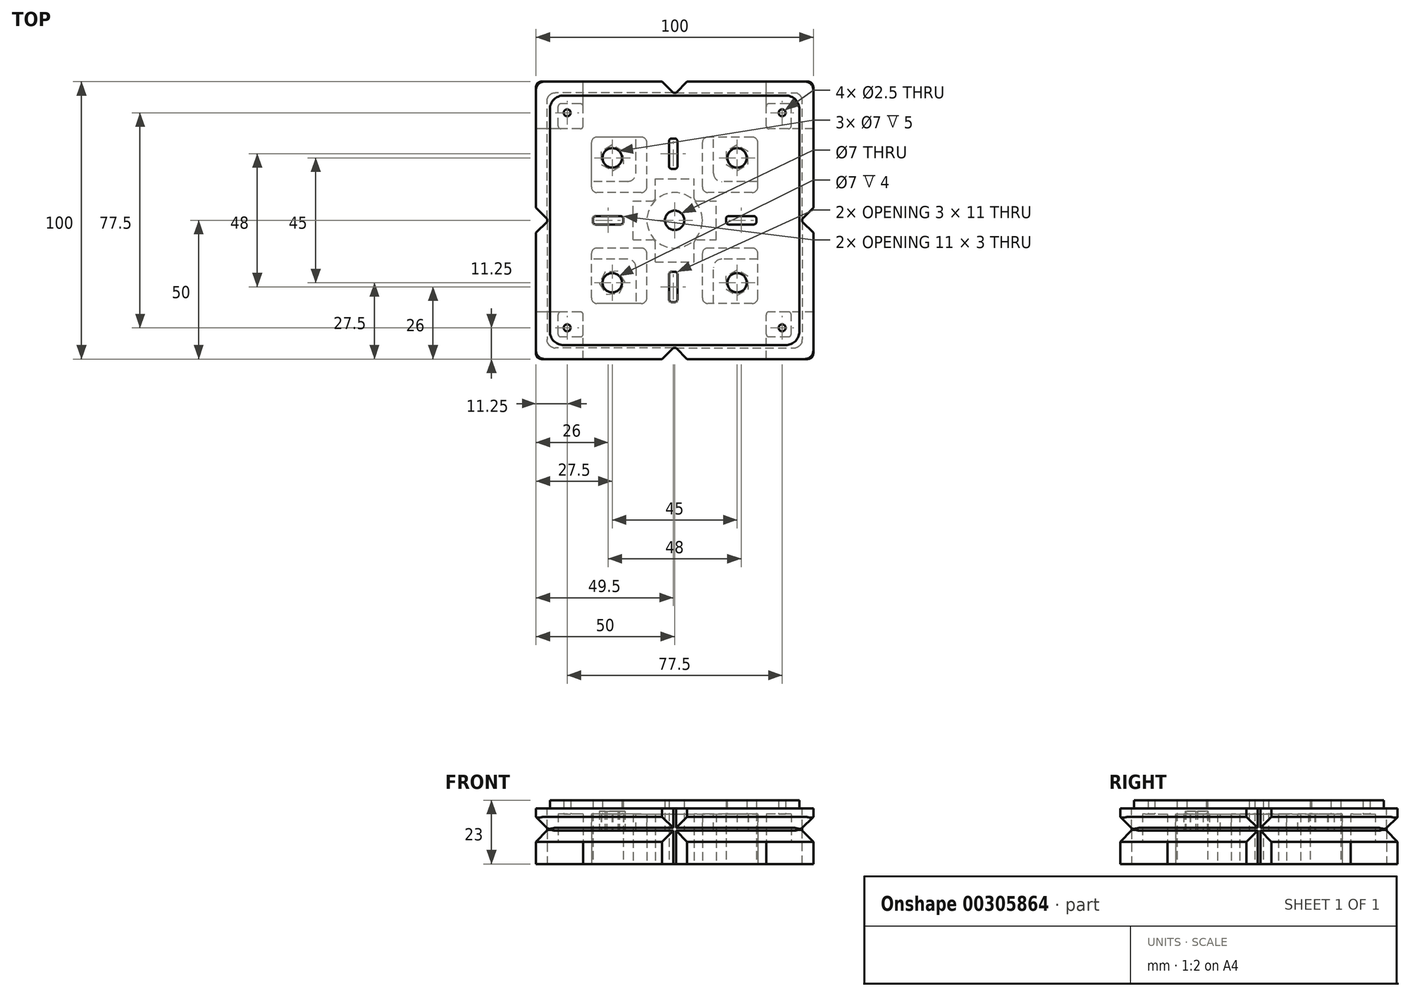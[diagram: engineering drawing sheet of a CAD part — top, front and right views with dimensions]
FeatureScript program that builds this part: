
annotation { "Feature Type Name" : "Feature", "Feature Type Description" : "" }
export const myFeature = defineFeature(function(context is Context, id is Id, definition is map)
    precondition{}
    {
        {
            var Q0;
            Q0=qCreatedBy(makeId("Top.planeOp"),FACE);
            var sketch = newSketch(context, id + "F0", { "sketchPlane" : qUnion([Q0])});
            skLineSegment(sketch, "E0.bottom", {"start": v(50, 50) * mm, "end": v(-50, 50) * mm});
            skLineSegment(sketch, "E0.top", {"start": v(50, -50) * mm, "end": v(-50, -50) * mm});
            skLineSegment(sketch, "E0.left", {"start": v(50, 50) * mm, "end": v(50, -50) * mm});
            skLineSegment(sketch, "E0.right", {"start": v(-50, 50) * mm, "end": v(-50, -50) * mm});
            skPoint(sketch, "E0.middle", {"position": v(0, 0) * mm});
            skCircle(sketch, "E1", {"center": v(0, 0) * mm, "radius": 3.5 * mm});
            skLineSegment(sketch, "E2.bottom", {"start": v(-4.5, -50) * mm, "end": v(4.5, -50) * mm});
            skLineSegment(sketch, "E2.top", {"start": v(-4.5, -46) * mm, "end": v(4.5, -46) * mm});
            skLineSegment(sketch, "E2.left", {"start": v(-4.5, -50) * mm, "end": v(-4.5, -46) * mm});
            skLineSegment(sketch, "E2.right", {"start": v(4.5, -50) * mm, "end": v(4.5, -46) * mm});
            skSolve(sketch);
        }
        {
            var Q0;
            Q0=qSketchRegion(id+"F0",true);
            extrude(context, id + "F1", {"entities" : qUnion([Q0]), "depth" : 20 * mm});
        }
        {
            var Q0;
            Q0=makeQuery(id+"F1.opExtrude","CAP_FACE",FACE,{"disambiguationData":[OSD([sQuery(id+"F0.wireOp",EDGE,"E0.bottom"),sQuery(id+"F0.wireOp",EDGE,"E0.top"),sQuery(id+"F0.wireOp",EDGE,"E0.left"),sQuery(id+"F0.wireOp",EDGE,"E0.right")])],"isStart":false});
            var sketch = newSketch(context, id + "F2", { "sketchPlane" : qUnion([Q0])});
            skLineSegment(sketch, "E3.bottom", {"start": v(45, 45) * mm, "end": v(-45, 45) * mm});
            skLineSegment(sketch, "E3.top", {"start": v(45, -45) * mm, "end": v(-45, -45) * mm});
            skLineSegment(sketch, "E3.left", {"start": v(45, 45) * mm, "end": v(45, -45) * mm});
            skLineSegment(sketch, "E3.right", {"start": v(-45, 45) * mm, "end": v(-45, -45) * mm});
            skPoint(sketch, "E3.middle", {"position": v(0, 0) * mm});
            skCircle(sketch, "E4", {"center": v(0, 0) * mm, "radius": 3.5 * mm});
            skLineSegment(sketch, "E5.bottom", {"start": v(-2, 29.5) * mm, "end": v(1, 29.5) * mm});
            skLineSegment(sketch, "E5.top", {"start": v(-2, 18.5) * mm, "end": v(1, 18.5) * mm});
            skLineSegment(sketch, "E5.left", {"start": v(-2, 29.5) * mm, "end": v(-2, 18.5) * mm});
            skLineSegment(sketch, "E5.right", {"start": v(1, 29.5) * mm, "end": v(1, 18.5) * mm});
            skLineSegment(sketch, "E6.bottom", {"start": v(-2, -18.5) * mm, "end": v(1, -18.5) * mm});
            skLineSegment(sketch, "E6.top", {"start": v(-2, -29.5) * mm, "end": v(1, -29.5) * mm});
            skLineSegment(sketch, "E6.left", {"start": v(-2, -18.5) * mm, "end": v(-2, -29.5) * mm});
            skLineSegment(sketch, "E6.right", {"start": v(1, -18.5) * mm, "end": v(1, -29.5) * mm});
            skLineSegment(sketch, "E7.bottom", {"start": v(-29.5, -1.5) * mm, "end": v(-29.5, 1.5) * mm});
            skLineSegment(sketch, "E7.top", {"start": v(-18.5, -1.5) * mm, "end": v(-18.5, 1.5) * mm});
            skLineSegment(sketch, "E7.left", {"start": v(-29.5, -1.5) * mm, "end": v(-18.5, -1.5) * mm});
            skLineSegment(sketch, "E7.right", {"start": v(-29.5, 1.5) * mm, "end": v(-18.5, 1.5) * mm});
            skLineSegment(sketch, "E8.bottom", {"start": v(18.5, -1.5) * mm, "end": v(18.5, 1.5) * mm});
            skLineSegment(sketch, "E8.top", {"start": v(29.5, -1.5) * mm, "end": v(29.5, 1.5) * mm});
            skLineSegment(sketch, "E8.left", {"start": v(18.5, -1.5) * mm, "end": v(29.5, -1.5) * mm});
            skLineSegment(sketch, "E8.right", {"start": v(18.5, 1.5) * mm, "end": v(29.5, 1.5) * mm});
            skCircle(sketch, "E9", {"center": v(22.5, -22.5) * mm, "radius": 3.5 * mm});
            skCircle(sketch, "E10", {"center": v(-22.5, -22.5) * mm, "radius": 3.5 * mm});
            skCircle(sketch, "E11", {"center": v(-22.5, 22.5) * mm, "radius": 3.5 * mm});
            skCircle(sketch, "E12", {"center": v(22.5, 22.5) * mm, "radius": 3.5 * mm});
            skCircle(sketch, "E13", {"center": v(-38.75, 38.75) * mm, "radius": 1.25 * mm});
            skCircle(sketch, "E14", {"center": v(38.75, 38.75) * mm, "radius": 1.25 * mm});
            skCircle(sketch, "E15", {"center": v(38.75, -38.75) * mm, "radius": 1.25 * mm});
            skCircle(sketch, "E16", {"center": v(-38.75, -38.75) * mm, "radius": 1.25 * mm});
            skSolve(sketch);
        }
        {
            var Q0;
            Q0=qSketchRegion(id+"F2",true);
            extrude(context, id + "F3", {"entities" : qUnion([Q0]), "operationType" : NewBodyOperationType.ADD, "depth" : 3 * mm});
        }
        {
            var Q0;
            Q0=makeQuery(id+"F3.boolean.opBoolean","SPLIT",FACE,{"disambiguationData":[TD([makeQuery(id+"F3.opExtrude","SWEPT_FACE",FACE,{"disambiguationData":[OSD([sQuery(id+"F2.wireOp",EDGE,"E5.bottom")])]})])],"derivedFrom":makeQuery(id+"F1.opExtrude","CAP_FACE",FACE,{"disambiguationData":[OSD([sQuery(id+"F0.wireOp",EDGE,"E0.bottom"),sQuery(id+"F0.wireOp",EDGE,"E0.top"),sQuery(id+"F0.wireOp",EDGE,"E0.left"),sQuery(id+"F0.wireOp",EDGE,"E0.right"),sQuery(id+"F0.wireOp",EDGE,"E1")])],"isStart":false})});
            extrude(context, id + "F4", {"entities" : qUnion([Q0]), "operationType" : NewBodyOperationType.REMOVE, "oppositeDirection" : true, "depth" : 25 * mm});
        }
        {
            var Q0;
            Q0=makeQuery(id+"F3.boolean.opBoolean","SPLIT",FACE,{"disambiguationData":[TD([makeQuery(id+"F3.opExtrude","SWEPT_FACE",FACE,{"disambiguationData":[OSD([sQuery(id+"F2.wireOp",EDGE,"E7.bottom")])]})])],"derivedFrom":makeQuery(id+"F1.opExtrude","CAP_FACE",FACE,{"disambiguationData":[OSD([sQuery(id+"F0.wireOp",EDGE,"E0.bottom"),sQuery(id+"F0.wireOp",EDGE,"E0.top"),sQuery(id+"F0.wireOp",EDGE,"E0.left"),sQuery(id+"F0.wireOp",EDGE,"E0.right"),sQuery(id+"F0.wireOp",EDGE,"E1")])],"isStart":false})});
            extrude(context, id + "F5", {"entities" : qUnion([Q0]), "operationType" : NewBodyOperationType.REMOVE, "oppositeDirection" : true, "depth" : 25 * mm});
        }
        {
            var Q0;
            Q0=makeQuery(id+"F3.boolean.opBoolean","SPLIT",FACE,{"disambiguationData":[TD([makeQuery(id+"F3.opExtrude","SWEPT_FACE",FACE,{"disambiguationData":[OSD([sQuery(id+"F2.wireOp",EDGE,"E6.bottom")])]})])],"derivedFrom":makeQuery(id+"F1.opExtrude","CAP_FACE",FACE,{"disambiguationData":[OSD([sQuery(id+"F0.wireOp",EDGE,"E0.bottom"),sQuery(id+"F0.wireOp",EDGE,"E0.top"),sQuery(id+"F0.wireOp",EDGE,"E0.left"),sQuery(id+"F0.wireOp",EDGE,"E0.right"),sQuery(id+"F0.wireOp",EDGE,"E1")])],"isStart":false})});
            extrude(context, id + "F6", {"entities" : qUnion([Q0]), "operationType" : NewBodyOperationType.REMOVE, "oppositeDirection" : true, "depth" : 25 * mm});
        }
        {
            var Q0;
            Q0=makeQuery(id+"F3.boolean.opBoolean","SPLIT",FACE,{"disambiguationData":[TD([makeQuery(id+"F3.opExtrude","SWEPT_FACE",FACE,{"disambiguationData":[OSD([sQuery(id+"F2.wireOp",EDGE,"E8.bottom")])]})])],"derivedFrom":makeQuery(id+"F1.opExtrude","CAP_FACE",FACE,{"disambiguationData":[OSD([sQuery(id+"F0.wireOp",EDGE,"E0.bottom"),sQuery(id+"F0.wireOp",EDGE,"E0.top"),sQuery(id+"F0.wireOp",EDGE,"E0.left"),sQuery(id+"F0.wireOp",EDGE,"E0.right"),sQuery(id+"F0.wireOp",EDGE,"E1")])],"isStart":false})});
            extrude(context, id + "F7", {"entities" : qUnion([Q0]), "operationType" : NewBodyOperationType.REMOVE, "oppositeDirection" : true, "depth" : 25 * mm});
        }
        {
            var Q0;
            {var subQ0=sQuery(id+"F2.wireOp",EDGE,"E5.left");var subQ1=sQuery(id+"F2.wireOp",EDGE,"E5.bottom");Q0=makeQuery(id+"F4.boolean.opBoolean","MERGE",EDGE,{"derivedFrom":[makeQuery(id+"F3.opExtrude","SWEPT_EDGE",EDGE,{"disambiguationData":[OSD([subQ1,subQ0])]}),makeQuery(id+"F4.opExtrude","SWEPT_EDGE",EDGE,{"disambiguationData":[OSD([subQ1,subQ0])]})]});}
            var Q1;
            {var subQ0=sQuery(id+"F2.wireOp",EDGE,"E5.right");var subQ1=sQuery(id+"F2.wireOp",EDGE,"E5.bottom");Q1=makeQuery(id+"F4.boolean.opBoolean","MERGE",EDGE,{"derivedFrom":[makeQuery(id+"F3.opExtrude","SWEPT_EDGE",EDGE,{"disambiguationData":[OSD([subQ1,subQ0])]}),makeQuery(id+"F4.opExtrude","SWEPT_EDGE",EDGE,{"disambiguationData":[OSD([subQ1,subQ0])]})]});}
            var Q2;
            {var subQ0=sQuery(id+"F2.wireOp",EDGE,"E5.right");var subQ1=sQuery(id+"F2.wireOp",EDGE,"E5.top");Q2=makeQuery(id+"F4.boolean.opBoolean","MERGE",EDGE,{"derivedFrom":[makeQuery(id+"F3.opExtrude","SWEPT_EDGE",EDGE,{"disambiguationData":[OSD([subQ1,subQ0])]}),makeQuery(id+"F4.opExtrude","SWEPT_EDGE",EDGE,{"disambiguationData":[OSD([subQ1,subQ0])]})]});}
            var Q3;
            {var subQ0=sQuery(id+"F2.wireOp",EDGE,"E5.left");var subQ1=sQuery(id+"F2.wireOp",EDGE,"E5.top");Q3=makeQuery(id+"F4.boolean.opBoolean","MERGE",EDGE,{"derivedFrom":[makeQuery(id+"F3.opExtrude","SWEPT_EDGE",EDGE,{"disambiguationData":[OSD([subQ1,subQ0])]}),makeQuery(id+"F4.opExtrude","SWEPT_EDGE",EDGE,{"disambiguationData":[OSD([subQ1,subQ0])]})]});}
            var Q4;
            {var subQ0=sQuery(id+"F2.wireOp",EDGE,"E8.right");var subQ1=sQuery(id+"F2.wireOp",EDGE,"E8.bottom");Q4=makeQuery(id+"F7.boolean.opBoolean","MERGE",EDGE,{"derivedFrom":[makeQuery(id+"F3.opExtrude","SWEPT_EDGE",EDGE,{"disambiguationData":[OSD([subQ1,subQ0])]}),makeQuery(id+"F7.opExtrude","SWEPT_EDGE",EDGE,{"disambiguationData":[OSD([subQ1,subQ0])]})]});}
            var Q5;
            {var subQ0=sQuery(id+"F2.wireOp",EDGE,"E8.left");var subQ1=sQuery(id+"F2.wireOp",EDGE,"E8.bottom");Q5=makeQuery(id+"F7.boolean.opBoolean","MERGE",EDGE,{"derivedFrom":[makeQuery(id+"F3.opExtrude","SWEPT_EDGE",EDGE,{"disambiguationData":[OSD([subQ1,subQ0])]}),makeQuery(id+"F7.opExtrude","SWEPT_EDGE",EDGE,{"disambiguationData":[OSD([subQ1,subQ0])]})]});}
            var Q6;
            {var subQ0=sQuery(id+"F2.wireOp",EDGE,"E8.left");var subQ1=sQuery(id+"F2.wireOp",EDGE,"E8.top");Q6=makeQuery(id+"F7.boolean.opBoolean","MERGE",EDGE,{"derivedFrom":[makeQuery(id+"F3.opExtrude","SWEPT_EDGE",EDGE,{"disambiguationData":[OSD([subQ1,subQ0])]}),makeQuery(id+"F7.opExtrude","SWEPT_EDGE",EDGE,{"disambiguationData":[OSD([subQ1,subQ0])]})]});}
            var Q7;
            {var subQ0=sQuery(id+"F2.wireOp",EDGE,"E8.right");var subQ1=sQuery(id+"F2.wireOp",EDGE,"E8.top");Q7=makeQuery(id+"F7.boolean.opBoolean","MERGE",EDGE,{"derivedFrom":[makeQuery(id+"F3.opExtrude","SWEPT_EDGE",EDGE,{"disambiguationData":[OSD([subQ1,subQ0])]}),makeQuery(id+"F7.opExtrude","SWEPT_EDGE",EDGE,{"disambiguationData":[OSD([subQ1,subQ0])]})]});}
            var Q8;
            {var subQ0=sQuery(id+"F2.wireOp",EDGE,"E6.right");var subQ1=sQuery(id+"F2.wireOp",EDGE,"E6.bottom");Q8=makeQuery(id+"F6.boolean.opBoolean","MERGE",EDGE,{"derivedFrom":[makeQuery(id+"F3.opExtrude","SWEPT_EDGE",EDGE,{"disambiguationData":[OSD([subQ1,subQ0])]}),makeQuery(id+"F6.opExtrude","SWEPT_EDGE",EDGE,{"disambiguationData":[OSD([subQ1,subQ0])]})]});}
            var Q9;
            {var subQ0=sQuery(id+"F2.wireOp",EDGE,"E6.left");var subQ1=sQuery(id+"F2.wireOp",EDGE,"E6.bottom");Q9=makeQuery(id+"F6.boolean.opBoolean","MERGE",EDGE,{"derivedFrom":[makeQuery(id+"F3.opExtrude","SWEPT_EDGE",EDGE,{"disambiguationData":[OSD([subQ1,subQ0])]}),makeQuery(id+"F6.opExtrude","SWEPT_EDGE",EDGE,{"disambiguationData":[OSD([subQ1,subQ0])]})]});}
            var Q10;
            {var subQ0=sQuery(id+"F2.wireOp",EDGE,"E6.left");var subQ1=sQuery(id+"F2.wireOp",EDGE,"E6.top");Q10=makeQuery(id+"F6.boolean.opBoolean","MERGE",EDGE,{"derivedFrom":[makeQuery(id+"F3.opExtrude","SWEPT_EDGE",EDGE,{"disambiguationData":[OSD([subQ1,subQ0])]}),makeQuery(id+"F6.opExtrude","SWEPT_EDGE",EDGE,{"disambiguationData":[OSD([subQ1,subQ0])]})]});}
            var Q11;
            {var subQ0=sQuery(id+"F2.wireOp",EDGE,"E6.right");var subQ1=sQuery(id+"F2.wireOp",EDGE,"E6.top");Q11=makeQuery(id+"F6.boolean.opBoolean","MERGE",EDGE,{"derivedFrom":[makeQuery(id+"F3.opExtrude","SWEPT_EDGE",EDGE,{"disambiguationData":[OSD([subQ1,subQ0])]}),makeQuery(id+"F6.opExtrude","SWEPT_EDGE",EDGE,{"disambiguationData":[OSD([subQ1,subQ0])]})]});}
            var Q12;
            {var subQ0=sQuery(id+"F2.wireOp",EDGE,"E7.left");var subQ1=sQuery(id+"F2.wireOp",EDGE,"E7.bottom");Q12=makeQuery(id+"F5.boolean.opBoolean","MERGE",EDGE,{"derivedFrom":[makeQuery(id+"F3.opExtrude","SWEPT_EDGE",EDGE,{"disambiguationData":[OSD([subQ1,subQ0])]}),makeQuery(id+"F5.opExtrude","SWEPT_EDGE",EDGE,{"disambiguationData":[OSD([subQ1,subQ0])]})]});}
            var Q13;
            {var subQ0=sQuery(id+"F2.wireOp",EDGE,"E7.right");var subQ1=sQuery(id+"F2.wireOp",EDGE,"E7.top");Q13=makeQuery(id+"F5.boolean.opBoolean","MERGE",EDGE,{"derivedFrom":[makeQuery(id+"F3.opExtrude","SWEPT_EDGE",EDGE,{"disambiguationData":[OSD([subQ1,subQ0])]}),makeQuery(id+"F5.opExtrude","SWEPT_EDGE",EDGE,{"disambiguationData":[OSD([subQ1,subQ0])]})]});}
            var Q14;
            {var subQ0=sQuery(id+"F2.wireOp",EDGE,"E7.left");var subQ1=sQuery(id+"F2.wireOp",EDGE,"E7.top");Q14=makeQuery(id+"F5.boolean.opBoolean","MERGE",EDGE,{"derivedFrom":[makeQuery(id+"F3.opExtrude","SWEPT_EDGE",EDGE,{"disambiguationData":[OSD([subQ1,subQ0])]}),makeQuery(id+"F5.opExtrude","SWEPT_EDGE",EDGE,{"disambiguationData":[OSD([subQ1,subQ0])]})]});}
            var Q15;
            {var subQ0=sQuery(id+"F2.wireOp",EDGE,"E7.right");var subQ1=sQuery(id+"F2.wireOp",EDGE,"E7.bottom");Q15=makeQuery(id+"F5.boolean.opBoolean","MERGE",EDGE,{"derivedFrom":[makeQuery(id+"F3.opExtrude","SWEPT_EDGE",EDGE,{"disambiguationData":[OSD([subQ1,subQ0])]}),makeQuery(id+"F5.opExtrude","SWEPT_EDGE",EDGE,{"disambiguationData":[OSD([subQ1,subQ0])]})]});}
            fillet(context, id + "F8", {"entities" : qUnion([Q0, Q1, Q2, Q3, Q4, Q5, Q6, Q7, Q8, Q9, Q10, Q11, Q12, Q13, Q14, Q15]), "radius" : 1 * mm, "tangentPropagation" : true, "allowEdgeOverflow" : false});
        }
        {
            var Q0;
            Q0=makeQuery(id+"F3.boolean.opBoolean","SPLIT",FACE,{"disambiguationData":[TD([makeQuery(id+"F3.opExtrude","SWEPT_FACE",FACE,{"disambiguationData":[OSD([sQuery(id+"F2.wireOp",EDGE,"E11")])]})])],"derivedFrom":makeQuery(id+"F1.opExtrude","CAP_FACE",FACE,{"disambiguationData":[OSD([sQuery(id+"F0.wireOp",EDGE,"E0.bottom"),sQuery(id+"F0.wireOp",EDGE,"E0.top"),sQuery(id+"F0.wireOp",EDGE,"E0.left"),sQuery(id+"F0.wireOp",EDGE,"E0.right"),sQuery(id+"F0.wireOp",EDGE,"E1")])],"isStart":false})});
            var Q1;
            Q1=makeQuery(id+"F3.boolean.opBoolean","SPLIT",FACE,{"disambiguationData":[TD([makeQuery(id+"F3.opExtrude","SWEPT_FACE",FACE,{"disambiguationData":[OSD([sQuery(id+"F2.wireOp",EDGE,"E12")])]})])],"derivedFrom":makeQuery(id+"F1.opExtrude","CAP_FACE",FACE,{"disambiguationData":[OSD([sQuery(id+"F0.wireOp",EDGE,"E0.bottom"),sQuery(id+"F0.wireOp",EDGE,"E0.top"),sQuery(id+"F0.wireOp",EDGE,"E0.left"),sQuery(id+"F0.wireOp",EDGE,"E0.right"),sQuery(id+"F0.wireOp",EDGE,"E1")])],"isStart":false})});
            var Q2;
            Q2=makeQuery(id+"F3.boolean.opBoolean","SPLIT",FACE,{"disambiguationData":[TD([makeQuery(id+"F3.opExtrude","SWEPT_FACE",FACE,{"disambiguationData":[OSD([sQuery(id+"F2.wireOp",EDGE,"E9")])]})])],"derivedFrom":makeQuery(id+"F1.opExtrude","CAP_FACE",FACE,{"disambiguationData":[OSD([sQuery(id+"F0.wireOp",EDGE,"E0.bottom"),sQuery(id+"F0.wireOp",EDGE,"E0.top"),sQuery(id+"F0.wireOp",EDGE,"E0.left"),sQuery(id+"F0.wireOp",EDGE,"E0.right"),sQuery(id+"F0.wireOp",EDGE,"E1")])],"isStart":false})});
            var Q3;
            Q3=makeQuery(id+"F3.boolean.opBoolean","SPLIT",FACE,{"disambiguationData":[TD([makeQuery(id+"F3.opExtrude","SWEPT_FACE",FACE,{"disambiguationData":[OSD([sQuery(id+"F2.wireOp",EDGE,"E10")])]})])],"derivedFrom":makeQuery(id+"F1.opExtrude","CAP_FACE",FACE,{"disambiguationData":[OSD([sQuery(id+"F0.wireOp",EDGE,"E0.bottom"),sQuery(id+"F0.wireOp",EDGE,"E0.top"),sQuery(id+"F0.wireOp",EDGE,"E0.left"),sQuery(id+"F0.wireOp",EDGE,"E0.right"),sQuery(id+"F0.wireOp",EDGE,"E1")])],"isStart":false})});
            extrude(context, id + "F9", {"entities" : qUnion([Q0, Q1, Q2, Q3]), "operationType" : NewBodyOperationType.REMOVE, "oppositeDirection" : true, "depth" : 25 * mm});
        }
        {
            var Q0;
            Q0=makeQuery(id+"F3.boolean.opBoolean","SPLIT",FACE,{"disambiguationData":[TD([makeQuery(id+"F3.opExtrude","SWEPT_FACE",FACE,{"disambiguationData":[OSD([sQuery(id+"F2.wireOp",EDGE,"E15")])]})])],"derivedFrom":makeQuery(id+"F1.opExtrude","CAP_FACE",FACE,{"disambiguationData":[OSD([sQuery(id+"F0.wireOp",EDGE,"E0.bottom"),sQuery(id+"F0.wireOp",EDGE,"E0.top"),sQuery(id+"F0.wireOp",EDGE,"E0.left"),sQuery(id+"F0.wireOp",EDGE,"E0.right"),sQuery(id+"F0.wireOp",EDGE,"E1")])],"isStart":false})});
            var Q1;
            Q1=makeQuery(id+"F3.boolean.opBoolean","SPLIT",FACE,{"disambiguationData":[TD([makeQuery(id+"F3.opExtrude","SWEPT_FACE",FACE,{"disambiguationData":[OSD([sQuery(id+"F2.wireOp",EDGE,"E16")])]})])],"derivedFrom":makeQuery(id+"F1.opExtrude","CAP_FACE",FACE,{"disambiguationData":[OSD([sQuery(id+"F0.wireOp",EDGE,"E0.bottom"),sQuery(id+"F0.wireOp",EDGE,"E0.top"),sQuery(id+"F0.wireOp",EDGE,"E0.left"),sQuery(id+"F0.wireOp",EDGE,"E0.right"),sQuery(id+"F0.wireOp",EDGE,"E1")])],"isStart":false})});
            var Q2;
            Q2=makeQuery(id+"F3.boolean.opBoolean","SPLIT",FACE,{"disambiguationData":[TD([makeQuery(id+"F3.opExtrude","SWEPT_FACE",FACE,{"disambiguationData":[OSD([sQuery(id+"F2.wireOp",EDGE,"E13")])]})])],"derivedFrom":makeQuery(id+"F1.opExtrude","CAP_FACE",FACE,{"disambiguationData":[OSD([sQuery(id+"F0.wireOp",EDGE,"E0.bottom"),sQuery(id+"F0.wireOp",EDGE,"E0.top"),sQuery(id+"F0.wireOp",EDGE,"E0.left"),sQuery(id+"F0.wireOp",EDGE,"E0.right"),sQuery(id+"F0.wireOp",EDGE,"E1")])],"isStart":false})});
            var Q3;
            Q3=makeQuery(id+"F3.boolean.opBoolean","SPLIT",FACE,{"disambiguationData":[TD([makeQuery(id+"F3.opExtrude","SWEPT_FACE",FACE,{"disambiguationData":[OSD([sQuery(id+"F2.wireOp",EDGE,"E14")])]})])],"derivedFrom":makeQuery(id+"F1.opExtrude","CAP_FACE",FACE,{"disambiguationData":[OSD([sQuery(id+"F0.wireOp",EDGE,"E0.bottom"),sQuery(id+"F0.wireOp",EDGE,"E0.top"),sQuery(id+"F0.wireOp",EDGE,"E0.left"),sQuery(id+"F0.wireOp",EDGE,"E0.right"),sQuery(id+"F0.wireOp",EDGE,"E1")])],"isStart":false})});
            extrude(context, id + "F10", {"entities" : qUnion([Q0, Q1, Q2, Q3]), "operationType" : NewBodyOperationType.REMOVE, "oppositeDirection" : true, "depth" : 25 * mm});
        }
        {
            var Q0;
            Q0=makeQuery(id+"F3.opExtrude","SWEPT_EDGE",EDGE,{"disambiguationData":[OSD([sQuery(id+"F2.wireOp",EDGE,"E3.top"),sQuery(id+"F2.wireOp",EDGE,"E3.right")])]});
            var Q1;
            Q1=makeQuery(id+"F3.opExtrude","SWEPT_EDGE",EDGE,{"disambiguationData":[OSD([sQuery(id+"F2.wireOp",EDGE,"E3.top"),sQuery(id+"F2.wireOp",EDGE,"E3.left")])]});
            var Q2;
            Q2=makeQuery(id+"F3.opExtrude","SWEPT_EDGE",EDGE,{"disambiguationData":[OSD([sQuery(id+"F2.wireOp",EDGE,"E3.bottom"),sQuery(id+"F2.wireOp",EDGE,"E3.right")])]});
            var Q3;
            Q3=makeQuery(id+"F3.opExtrude","SWEPT_EDGE",EDGE,{"disambiguationData":[OSD([sQuery(id+"F2.wireOp",EDGE,"E3.bottom"),sQuery(id+"F2.wireOp",EDGE,"E3.left")])]});
            fillet(context, id + "F11", {"entities" : qUnion([Q0, Q1, Q2, Q3]), "radius" : 5 * mm, "tangentPropagation" : true, "allowEdgeOverflow" : false});
        }
        {
            var Q0;
            Q0=makeQuery(id+"F1.opExtrude","CAP_FACE",FACE,{"disambiguationData":[OSD([sQuery(id+"F0.wireOp",EDGE,"E0.bottom"),sQuery(id+"F0.wireOp",EDGE,"E0.top"),sQuery(id+"F0.wireOp",EDGE,"E0.left"),sQuery(id+"F0.wireOp",EDGE,"E0.right"),sQuery(id+"F0.wireOp",EDGE,"E1"),sQuery(id+"F0.wireOp",EDGE,"E2.bottom")])],"isStart":true});
            var sketch = newSketch(context, id + "F12", { "sketchPlane" : qUnion([Q0])});
            skLineSegment(sketch, "E17.bottom", {"start": v(-4.5, 50) * mm, "end": v(4.5, 50) * mm});
            skLineSegment(sketch, "E17.top", {"start": v(-4.5, 46) * mm, "end": v(4.5, 46) * mm});
            skLineSegment(sketch, "E17.left", {"start": v(-4.5, 50) * mm, "end": v(-4.5, 46) * mm});
            skLineSegment(sketch, "E17.right", {"start": v(4.5, 50) * mm, "end": v(4.5, 46) * mm});
            skLineSegment(sketch, "E18.bottom", {"start": v(-46, 4.5) * mm, "end": v(-50, 4.5) * mm});
            skLineSegment(sketch, "E18.top", {"start": v(-46, -4.5) * mm, "end": v(-50, -4.5) * mm});
            skLineSegment(sketch, "E18.left", {"start": v(-46, 4.5) * mm, "end": v(-46, -4.5) * mm});
            skLineSegment(sketch, "E18.right", {"start": v(-50, 4.5) * mm, "end": v(-50, -4.5) * mm});
            skLineSegment(sketch, "E19.bottom", {"start": v(46, 4.5) * mm, "end": v(50, 4.5) * mm});
            skLineSegment(sketch, "E19.top", {"start": v(46, -4.5) * mm, "end": v(50, -4.5) * mm});
            skLineSegment(sketch, "E19.left", {"start": v(46, 4.5) * mm, "end": v(46, -4.5) * mm});
            skLineSegment(sketch, "E19.right", {"start": v(50, 4.5) * mm, "end": v(50, -4.5) * mm});
            skLineSegment(sketch, "E20.bottom", {"start": v(-4.5, -50) * mm, "end": v(4.5, -50) * mm});
            skLineSegment(sketch, "E20.top", {"start": v(-4.5, -46) * mm, "end": v(4.5, -46) * mm});
            skLineSegment(sketch, "E20.left", {"start": v(-4.5, -50) * mm, "end": v(-4.5, -46) * mm});
            skLineSegment(sketch, "E20.right", {"start": v(4.5, -50) * mm, "end": v(4.5, -46) * mm});
            skSolve(sketch);
        }
        {
            var Q0;
            Q0=qSketchRegion(id+"F12",true);
            extrude(context, id + "F13", {"entities" : qUnion([Q0]), "operationType" : NewBodyOperationType.REMOVE, "oppositeDirection" : true, "depth" : 25 * mm});
        }
        {
            var Q0;
            Q0=makeQuery(id+"F13.boolean.opBoolean","COPY",EDGE,{"derivedFrom":makeQuery(id+"F13.opExtrude","SWEPT_EDGE",EDGE,{"disambiguationData":[OSD([sQuery(id+"F12.wireOp",EDGE,"E20.top"),sQuery(id+"F12.wireOp",EDGE,"E20.left")])]})});
            var Q1;
            Q1=makeQuery(id+"F13.boolean.opBoolean","COPY",EDGE,{"derivedFrom":makeQuery(id+"F13.opExtrude","SWEPT_EDGE",EDGE,{"disambiguationData":[OSD([sQuery(id+"F12.wireOp",EDGE,"E20.top"),sQuery(id+"F12.wireOp",EDGE,"E20.right")])]})});
            chamfer(context, id + "F14", {"entities" : qUnion([Q0, Q1]), "width" : 4 * mm, "tangentPropagation" : true});
        }
        {
            var Q0;
            Q0=makeQuery(id+"F13.boolean.opBoolean","COPY",EDGE,{"derivedFrom":makeQuery(id+"F13.opExtrude","SWEPT_EDGE",EDGE,{"disambiguationData":[OSD([sQuery(id+"F12.wireOp",EDGE,"E18.bottom"),sQuery(id+"F12.wireOp",EDGE,"E18.left")])]})});
            var Q1;
            Q1=makeQuery(id+"F13.boolean.opBoolean","COPY",EDGE,{"derivedFrom":makeQuery(id+"F13.opExtrude","SWEPT_EDGE",EDGE,{"disambiguationData":[OSD([sQuery(id+"F12.wireOp",EDGE,"E18.top"),sQuery(id+"F12.wireOp",EDGE,"E18.left")])]})});
            var Q2;
            Q2=makeQuery(id+"F13.boolean.opBoolean","COPY",EDGE,{"derivedFrom":makeQuery(id+"F13.opExtrude","SWEPT_EDGE",EDGE,{"disambiguationData":[OSD([sQuery(id+"F12.wireOp",EDGE,"E19.top"),sQuery(id+"F12.wireOp",EDGE,"E19.left")])]})});
            var Q3;
            Q3=makeQuery(id+"F13.boolean.opBoolean","COPY",EDGE,{"derivedFrom":makeQuery(id+"F13.opExtrude","SWEPT_EDGE",EDGE,{"disambiguationData":[OSD([sQuery(id+"F12.wireOp",EDGE,"E19.bottom"),sQuery(id+"F12.wireOp",EDGE,"E19.left")])]})});
            var Q4;
            Q4=makeQuery(id+"F13.boolean.opBoolean","COPY",EDGE,{"derivedFrom":makeQuery(id+"F13.opExtrude","SWEPT_EDGE",EDGE,{"disambiguationData":[OSD([sQuery(id+"F12.wireOp",EDGE,"E17.top"),sQuery(id+"F12.wireOp",EDGE,"E17.right")])]})});
            var Q5;
            Q5=makeQuery(id+"F13.boolean.opBoolean","COPY",EDGE,{"derivedFrom":makeQuery(id+"F13.opExtrude","SWEPT_EDGE",EDGE,{"disambiguationData":[OSD([sQuery(id+"F12.wireOp",EDGE,"E17.top"),sQuery(id+"F12.wireOp",EDGE,"E17.left")])]})});
            chamfer(context, id + "F15", {"entities" : qUnion([Q0, Q1, Q2, Q3, Q4, Q5]), "width" : 4 * mm, "tangentPropagation" : true});
        }
        {
            var Q0;
            {var subQ0=sQuery(id+"F0.wireOp",EDGE,"E2.bottom");var subQ2=sQuery(id+"F0.wireOp",EDGE,"E0.right");var subQ4=sQuery(id+"F0.wireOp",EDGE,"E0.top");Q0=makeQuery(id+"F13.boolean.opBoolean","SPLIT",FACE,{"disambiguationData":[TD([makeQuery(id+"F1.opExtrude","SWEPT_FACE",FACE,{"disambiguationData":[OSD([subQ2])]})])],"derivedFrom":makeQuery(id+"F1.opExtrude","SWEPT_FACE",FACE,{"disambiguationData":[OSD([subQ4,subQ0])]})});}
            var sketch = newSketch(context, id + "F16", { "sketchPlane" : qUnion([Q0])});
            skLineSegment(sketch, "E21.bottom", {"start": v(-50, 17) * mm, "end": v(50, 17) * mm});
            skLineSegment(sketch, "E21.top", {"start": v(-50, 8) * mm, "end": v(50, 8) * mm});
            skLineSegment(sketch, "E21.left", {"start": v(-50, 17) * mm, "end": v(-50, 8) * mm});
            skLineSegment(sketch, "E21.right", {"start": v(50, 17) * mm, "end": v(50, 8) * mm});
            skSolve(sketch);
        }
        {
            var Q0;
            Q0=qSketchRegion(id+"F16",true);
            extrude(context, id + "F17", {"entities" : qUnion([Q0]), "operationType" : NewBodyOperationType.REMOVE, "oppositeDirection" : true, "depth" : 4 * mm});
        }
        {
            var Q0;
            {var subQ0=sQuery(id+"F0.wireOp",EDGE,"E0.bottom");var subQ3=sQuery(id+"F0.wireOp",EDGE,"E0.right");Q0=makeQuery(id+"F13.boolean.opBoolean","SPLIT",FACE,{"disambiguationData":[TD([makeQuery(id+"F1.opExtrude","SWEPT_FACE",FACE,{"disambiguationData":[OSD([subQ0])]})])],"derivedFrom":makeQuery(id+"F1.opExtrude","SWEPT_FACE",FACE,{"disambiguationData":[OSD([subQ3])]})});}
            var sketch = newSketch(context, id + "F18", { "sketchPlane" : qUnion([Q0])});
            skLineSegment(sketch, "E22.bottom", {"start": v(-50, 17) * mm, "end": v(50, 17) * mm});
            skLineSegment(sketch, "E22.top", {"start": v(-50, 8) * mm, "end": v(50, 8) * mm});
            skLineSegment(sketch, "E22.left", {"start": v(-50, 17) * mm, "end": v(-50, 8) * mm});
            skLineSegment(sketch, "E22.right", {"start": v(50, 17) * mm, "end": v(50, 8) * mm});
            skSolve(sketch);
        }
        {
            var Q0;
            Q0=qSketchRegion(id+"F18",true);
            extrude(context, id + "F19", {"entities" : qUnion([Q0]), "operationType" : NewBodyOperationType.REMOVE, "oppositeDirection" : true, "depth" : 4 * mm});
        }
        {
            var Q0;
            {var subQ3=sQuery(id+"F0.wireOp",EDGE,"E0.left");var subQ5=sQuery(id+"F0.wireOp",EDGE,"E0.bottom");Q0=makeQuery(id+"F13.boolean.opBoolean","SPLIT",FACE,{"disambiguationData":[TD([makeQuery(id+"F1.opExtrude","SWEPT_FACE",FACE,{"disambiguationData":[OSD([subQ3])]})])],"derivedFrom":makeQuery(id+"F1.opExtrude","SWEPT_FACE",FACE,{"disambiguationData":[OSD([subQ5])]})});}
            var sketch = newSketch(context, id + "F20", { "sketchPlane" : qUnion([Q0])});
            skLineSegment(sketch, "E23.bottom", {"start": v(-50, 17) * mm, "end": v(50, 17) * mm});
            skLineSegment(sketch, "E23.top", {"start": v(-50, 8) * mm, "end": v(50, 8) * mm});
            skLineSegment(sketch, "E23.left", {"start": v(-50, 17) * mm, "end": v(-50, 8) * mm});
            skLineSegment(sketch, "E23.right", {"start": v(50, 17) * mm, "end": v(50, 8) * mm});
            skSolve(sketch);
        }
        {
            var Q0;
            Q0=qSketchRegion(id+"F20",true);
            extrude(context, id + "F21", {"entities" : qUnion([Q0]), "operationType" : NewBodyOperationType.REMOVE, "oppositeDirection" : true, "depth" : 4 * mm});
        }
        {
            var Q0;
            {var subQ3=sQuery(id+"F0.wireOp",EDGE,"E0.left");Q0=makeQuery(id+"F13.boolean.opBoolean","SPLIT",FACE,{"disambiguationData":[TD([makeQuery(id+"F13.opExtrude","SWEPT_FACE",FACE,{"disambiguationData":[OSD([sQuery(id+"F12.wireOp",EDGE,"E19.bottom")])]})])],"derivedFrom":makeQuery(id+"F1.opExtrude","SWEPT_FACE",FACE,{"disambiguationData":[OSD([subQ3])]})});}
            var sketch = newSketch(context, id + "F22", { "sketchPlane" : qUnion([Q0])});
            skLineSegment(sketch, "E24.bottom", {"start": v(-50, 17) * mm, "end": v(50, 17) * mm});
            skLineSegment(sketch, "E24.top", {"start": v(-50, 8) * mm, "end": v(50, 8) * mm});
            skLineSegment(sketch, "E24.left", {"start": v(-50, 17) * mm, "end": v(-50, 8) * mm});
            skLineSegment(sketch, "E24.right", {"start": v(50, 17) * mm, "end": v(50, 8) * mm});
            skSolve(sketch);
        }
        {
            var Q0;
            Q0=qSketchRegion(id+"F22",true);
            extrude(context, id + "F23", {"entities" : qUnion([Q0]), "operationType" : NewBodyOperationType.REMOVE, "oppositeDirection" : true, "depth" : 4 * mm});
        }
        {
            var Q0;
            {var subQ1=sQuery(id+"F16.wireOp",EDGE,"E21.bottom");Q0=makeQuery(id+"F17.boolean.opBoolean","COPY",EDGE,{"disambiguationData":[TD([makeQuery(id+"F1.opExtrude","SWEPT_FACE",FACE,{"disambiguationData":[OSD([sQuery(id+"F0.wireOp",EDGE,"E0.left")])]})])],"derivedFrom":makeQuery(id+"F17.opExtrude","CAP_EDGE",EDGE,{"disambiguationData":[OSD([subQ1])],"isStart":false})});}
            var Q1;
            {var subQ1=sQuery(id+"F16.wireOp",EDGE,"E21.bottom");var subQ2=sQuery(id+"F22.wireOp",EDGE,"E24.bottom");Q1=makeQuery(id+"F23.boolean.opBoolean","COPY",EDGE,{"disambiguationData":[topologyDisambiguationEdgeConnected([makeQuery(id+"F17.boolean.opBoolean","COPY",FACE,{"disambiguationData":[TD([makeQuery(id+"F1.opExtrude","SWEPT_FACE",FACE,{"disambiguationData":[OSD([sQuery(id+"F0.wireOp",EDGE,"E0.left")])]})])],"derivedFrom":makeQuery(id+"F17.opExtrude","SWEPT_FACE",FACE,{"disambiguationData":[OSD([subQ1])]})})])],"derivedFrom":makeQuery(id+"F23.opExtrude","CAP_EDGE",EDGE,{"disambiguationData":[OSD([subQ2])],"isStart":false})});}
            var Q2;
            {var subQ0=sQuery(id+"F22.wireOp",EDGE,"E24.bottom");Q2=makeQuery(id+"F23.boolean.opBoolean","COPY",EDGE,{"disambiguationData":[topologyDisambiguationEdgeConnected([makeQuery(id+"F21.boolean.opBoolean","COPY",FACE,{"derivedFrom":makeQuery(id+"F21.opExtrude","SWEPT_FACE",FACE,{"disambiguationData":[OSD([sQuery(id+"F20.wireOp",EDGE,"E23.bottom")])]})})])],"derivedFrom":makeQuery(id+"F23.opExtrude","CAP_EDGE",EDGE,{"disambiguationData":[OSD([subQ0])],"isStart":false})});}
            var Q3;
            {var subQ0=sQuery(id+"F20.wireOp",EDGE,"E23.bottom");Q3=makeQuery(id+"F21.boolean.opBoolean","COPY",EDGE,{"disambiguationData":[topologyDisambiguationEdgeConnected([makeQuery(id+"F13.boolean.opBoolean","COPY",FACE,{"derivedFrom":makeQuery(id+"F13.opExtrude","SWEPT_FACE",FACE,{"disambiguationData":[OSD([sQuery(id+"F12.wireOp",EDGE,"E20.top")])]})}),makeQuery(id+"F21.opExtrude","SWEPT_FACE",FACE,{"disambiguationData":[OSD([subQ0])]}),makeQuery(id+"F21.opExtrude","CAP_FACE",FACE,{"disambiguationData":[OSD([subQ0,sQuery(id+"F20.wireOp",EDGE,"E23.top"),sQuery(id+"F20.wireOp",EDGE,"E23.left"),sQuery(id+"F20.wireOp",EDGE,"E23.right")])],"isStart":false})])],"derivedFrom":makeQuery(id+"F21.opExtrude","CAP_EDGE",EDGE,{"disambiguationData":[OSD([subQ0])],"isStart":false})});}
            var Q4;
            {var subQ0=sQuery(id+"F22.wireOp",EDGE,"E24.top");Q4=makeQuery(id+"F23.boolean.opBoolean","COPY",EDGE,{"disambiguationData":[topologyDisambiguationEdgeConnected([makeQuery(id+"F21.boolean.opBoolean","COPY",FACE,{"derivedFrom":makeQuery(id+"F21.opExtrude","SWEPT_FACE",FACE,{"disambiguationData":[OSD([sQuery(id+"F20.wireOp",EDGE,"E23.top")])]})})])],"derivedFrom":makeQuery(id+"F23.opExtrude","CAP_EDGE",EDGE,{"disambiguationData":[OSD([subQ0])],"isStart":false})});}
            var Q5;
            {var subQ1=sQuery(id+"F16.wireOp",EDGE,"E21.top");var subQ2=sQuery(id+"F22.wireOp",EDGE,"E24.top");Q5=makeQuery(id+"F23.boolean.opBoolean","COPY",EDGE,{"disambiguationData":[topologyDisambiguationEdgeConnected([makeQuery(id+"F17.boolean.opBoolean","COPY",FACE,{"disambiguationData":[TD([makeQuery(id+"F1.opExtrude","SWEPT_FACE",FACE,{"disambiguationData":[OSD([sQuery(id+"F0.wireOp",EDGE,"E0.left")])]})])],"derivedFrom":makeQuery(id+"F17.opExtrude","SWEPT_FACE",FACE,{"disambiguationData":[OSD([subQ1])]})})])],"derivedFrom":makeQuery(id+"F23.opExtrude","CAP_EDGE",EDGE,{"disambiguationData":[OSD([subQ2])],"isStart":false})});}
            var Q6;
            {var subQ0=sQuery(id+"F20.wireOp",EDGE,"E23.top");Q6=makeQuery(id+"F21.boolean.opBoolean","COPY",EDGE,{"disambiguationData":[topologyDisambiguationEdgeConnected([makeQuery(id+"F13.boolean.opBoolean","COPY",FACE,{"derivedFrom":makeQuery(id+"F13.opExtrude","SWEPT_FACE",FACE,{"disambiguationData":[OSD([sQuery(id+"F12.wireOp",EDGE,"E20.top")])]})}),makeQuery(id+"F21.opExtrude","CAP_FACE",FACE,{"disambiguationData":[OSD([sQuery(id+"F20.wireOp",EDGE,"E23.bottom"),subQ0,sQuery(id+"F20.wireOp",EDGE,"E23.left"),sQuery(id+"F20.wireOp",EDGE,"E23.right")])],"isStart":false}),makeQuery(id+"F21.opExtrude","SWEPT_FACE",FACE,{"disambiguationData":[OSD([subQ0])]})])],"derivedFrom":makeQuery(id+"F21.opExtrude","CAP_EDGE",EDGE,{"disambiguationData":[OSD([subQ0])],"isStart":false})});}
            var Q7;
            {var subQ1=sQuery(id+"F16.wireOp",EDGE,"E21.top");var subQ2=sQuery(id+"F18.wireOp",EDGE,"E22.top");Q7=makeQuery(id+"F19.boolean.opBoolean","COPY",EDGE,{"disambiguationData":[topologyDisambiguationEdgeConnected([makeQuery(id+"F13.boolean.opBoolean","COPY",FACE,{"derivedFrom":makeQuery(id+"F13.opExtrude","SWEPT_FACE",FACE,{"disambiguationData":[OSD([sQuery(id+"F12.wireOp",EDGE,"E18.left")])]})}),makeQuery(id+"F17.boolean.opBoolean","COPY",FACE,{"disambiguationData":[TD([makeQuery(id+"F1.opExtrude","SWEPT_FACE",FACE,{"disambiguationData":[OSD([sQuery(id+"F0.wireOp",EDGE,"E0.right")])]})])],"derivedFrom":makeQuery(id+"F17.opExtrude","SWEPT_FACE",FACE,{"disambiguationData":[OSD([subQ1])]})}),makeQuery(id+"F19.opExtrude","CAP_FACE",FACE,{"disambiguationData":[OSD([sQuery(id+"F18.wireOp",EDGE,"E22.bottom"),subQ2,sQuery(id+"F18.wireOp",EDGE,"E22.left"),sQuery(id+"F18.wireOp",EDGE,"E22.right")])],"isStart":false}),makeQuery(id+"F19.opExtrude","SWEPT_FACE",FACE,{"disambiguationData":[OSD([subQ2])]})])],"derivedFrom":makeQuery(id+"F19.opExtrude","CAP_EDGE",EDGE,{"disambiguationData":[OSD([subQ2])],"isStart":false})});}
            var Q8;
            {var subQ0=sQuery(id+"F18.wireOp",EDGE,"E22.top");Q8=makeQuery(id+"F19.boolean.opBoolean","COPY",EDGE,{"disambiguationData":[topologyDisambiguationEdgeConnected([makeQuery(id+"F13.boolean.opBoolean","COPY",FACE,{"derivedFrom":makeQuery(id+"F13.opExtrude","SWEPT_FACE",FACE,{"disambiguationData":[OSD([sQuery(id+"F12.wireOp",EDGE,"E18.left")])]})}),makeQuery(id+"F19.opExtrude","CAP_FACE",FACE,{"disambiguationData":[OSD([sQuery(id+"F18.wireOp",EDGE,"E22.bottom"),subQ0,sQuery(id+"F18.wireOp",EDGE,"E22.left"),sQuery(id+"F18.wireOp",EDGE,"E22.right")])],"isStart":false}),makeQuery(id+"F19.opExtrude","SWEPT_FACE",FACE,{"disambiguationData":[OSD([subQ0])]})])],"derivedFrom":makeQuery(id+"F19.opExtrude","CAP_EDGE",EDGE,{"disambiguationData":[OSD([subQ0])],"isStart":false})});}
            var Q9;
            {var subQ0=sQuery(id+"F18.wireOp",EDGE,"E22.bottom");Q9=makeQuery(id+"F19.boolean.opBoolean","COPY",EDGE,{"disambiguationData":[topologyDisambiguationEdgeConnected([makeQuery(id+"F13.boolean.opBoolean","COPY",FACE,{"derivedFrom":makeQuery(id+"F13.opExtrude","SWEPT_FACE",FACE,{"disambiguationData":[OSD([sQuery(id+"F12.wireOp",EDGE,"E18.left")])]})}),makeQuery(id+"F19.opExtrude","SWEPT_FACE",FACE,{"disambiguationData":[OSD([subQ0])]}),makeQuery(id+"F19.opExtrude","CAP_FACE",FACE,{"disambiguationData":[OSD([subQ0,sQuery(id+"F18.wireOp",EDGE,"E22.top"),sQuery(id+"F18.wireOp",EDGE,"E22.left"),sQuery(id+"F18.wireOp",EDGE,"E22.right")])],"isStart":false})])],"derivedFrom":makeQuery(id+"F19.opExtrude","CAP_EDGE",EDGE,{"disambiguationData":[OSD([subQ0])],"isStart":false})});}
            var Q10;
            {var subQ1=sQuery(id+"F16.wireOp",EDGE,"E21.bottom");var subQ2=sQuery(id+"F18.wireOp",EDGE,"E22.bottom");Q10=makeQuery(id+"F19.boolean.opBoolean","COPY",EDGE,{"disambiguationData":[topologyDisambiguationEdgeConnected([makeQuery(id+"F13.boolean.opBoolean","COPY",FACE,{"derivedFrom":makeQuery(id+"F13.opExtrude","SWEPT_FACE",FACE,{"disambiguationData":[OSD([sQuery(id+"F12.wireOp",EDGE,"E18.left")])]})}),makeQuery(id+"F17.boolean.opBoolean","COPY",FACE,{"disambiguationData":[TD([makeQuery(id+"F1.opExtrude","SWEPT_FACE",FACE,{"disambiguationData":[OSD([sQuery(id+"F0.wireOp",EDGE,"E0.right")])]})])],"derivedFrom":makeQuery(id+"F17.opExtrude","SWEPT_FACE",FACE,{"disambiguationData":[OSD([subQ1])]})}),makeQuery(id+"F19.opExtrude","SWEPT_FACE",FACE,{"disambiguationData":[OSD([subQ2])]}),makeQuery(id+"F19.opExtrude","CAP_FACE",FACE,{"disambiguationData":[OSD([subQ2,sQuery(id+"F18.wireOp",EDGE,"E22.top"),sQuery(id+"F18.wireOp",EDGE,"E22.left"),sQuery(id+"F18.wireOp",EDGE,"E22.right")])],"isStart":false})])],"derivedFrom":makeQuery(id+"F19.opExtrude","CAP_EDGE",EDGE,{"disambiguationData":[OSD([subQ2])],"isStart":false})});}
            var Q11;
            {var subQ1=sQuery(id+"F16.wireOp",EDGE,"E21.bottom");Q11=makeQuery(id+"F17.boolean.opBoolean","COPY",EDGE,{"disambiguationData":[TD([makeQuery(id+"F1.opExtrude","SWEPT_FACE",FACE,{"disambiguationData":[OSD([sQuery(id+"F0.wireOp",EDGE,"E0.right")])]})])],"derivedFrom":makeQuery(id+"F17.opExtrude","CAP_EDGE",EDGE,{"disambiguationData":[OSD([subQ1])],"isStart":false})});}
            var Q12;
            {var subQ0=sQuery(id+"F16.wireOp",EDGE,"E21.top");Q12=makeQuery(id+"F17.boolean.opBoolean","COPY",EDGE,{"disambiguationData":[TD([makeQuery(id+"F1.opExtrude","SWEPT_FACE",FACE,{"disambiguationData":[OSD([sQuery(id+"F0.wireOp",EDGE,"E0.right")])]})])],"derivedFrom":makeQuery(id+"F17.opExtrude","CAP_EDGE",EDGE,{"disambiguationData":[OSD([subQ0])],"isStart":false})});}
            var Q13;
            {var subQ1=sQuery(id+"F16.wireOp",EDGE,"E21.top");Q13=makeQuery(id+"F17.boolean.opBoolean","COPY",EDGE,{"disambiguationData":[TD([makeQuery(id+"F1.opExtrude","SWEPT_FACE",FACE,{"disambiguationData":[OSD([sQuery(id+"F0.wireOp",EDGE,"E0.left")])]})])],"derivedFrom":makeQuery(id+"F17.opExtrude","CAP_EDGE",EDGE,{"disambiguationData":[OSD([subQ1])],"isStart":false})});}
            var Q14;
            {var subQ0=sQuery(id+"F20.wireOp",EDGE,"E23.top");Q14=makeQuery(id+"F21.boolean.opBoolean","COPY",EDGE,{"disambiguationData":[topologyDisambiguationEdgeConnected([makeQuery(id+"F13.boolean.opBoolean","COPY",FACE,{"derivedFrom":makeQuery(id+"F13.opExtrude","SWEPT_FACE",FACE,{"disambiguationData":[OSD([sQuery(id+"F12.wireOp",EDGE,"E20.top")])]})}),makeQuery(id+"F19.boolean.opBoolean","COPY",FACE,{"derivedFrom":makeQuery(id+"F19.opExtrude","SWEPT_FACE",FACE,{"disambiguationData":[OSD([sQuery(id+"F18.wireOp",EDGE,"E22.top")])]})}),makeQuery(id+"F21.opExtrude","CAP_FACE",FACE,{"disambiguationData":[OSD([sQuery(id+"F20.wireOp",EDGE,"E23.bottom"),subQ0,sQuery(id+"F20.wireOp",EDGE,"E23.left"),sQuery(id+"F20.wireOp",EDGE,"E23.right")])],"isStart":false}),makeQuery(id+"F21.opExtrude","SWEPT_FACE",FACE,{"disambiguationData":[OSD([subQ0])]})])],"derivedFrom":makeQuery(id+"F21.opExtrude","CAP_EDGE",EDGE,{"disambiguationData":[OSD([subQ0])],"isStart":false})});}
            var Q15;
            {var subQ0=sQuery(id+"F20.wireOp",EDGE,"E23.bottom");Q15=makeQuery(id+"F21.boolean.opBoolean","COPY",EDGE,{"disambiguationData":[topologyDisambiguationEdgeConnected([makeQuery(id+"F13.boolean.opBoolean","COPY",FACE,{"derivedFrom":makeQuery(id+"F13.opExtrude","SWEPT_FACE",FACE,{"disambiguationData":[OSD([sQuery(id+"F12.wireOp",EDGE,"E20.top")])]})}),makeQuery(id+"F19.boolean.opBoolean","COPY",FACE,{"derivedFrom":makeQuery(id+"F19.opExtrude","SWEPT_FACE",FACE,{"disambiguationData":[OSD([sQuery(id+"F18.wireOp",EDGE,"E22.bottom")])]})}),makeQuery(id+"F21.opExtrude","SWEPT_FACE",FACE,{"disambiguationData":[OSD([subQ0])]}),makeQuery(id+"F21.opExtrude","CAP_FACE",FACE,{"disambiguationData":[OSD([subQ0,sQuery(id+"F20.wireOp",EDGE,"E23.top"),sQuery(id+"F20.wireOp",EDGE,"E23.left"),sQuery(id+"F20.wireOp",EDGE,"E23.right")])],"isStart":false})])],"derivedFrom":makeQuery(id+"F21.opExtrude","CAP_EDGE",EDGE,{"disambiguationData":[OSD([subQ0])],"isStart":false})});}
            chamfer(context, id + "F24", {"entities" : qUnion([Q0, Q1, Q2, Q3, Q4, Q5, Q6, Q7, Q8, Q9, Q10, Q11, Q12, Q13, Q14, Q15]), "width" : 4 * mm, "tangentPropagation" : true});
        }
        {
            var Q0;
            {var subQ3=sQuery(id+"F16.wireOp",EDGE,"E21.bottom");var subQ5=makeQuery(id+"F1.opExtrude","SWEPT_FACE",FACE,{"disambiguationData":[OSD([sQuery(id+"F0.wireOp",EDGE,"E0.left")])]});var subQ6=makeQuery(id+"F17.opExtrude","SWEPT_FACE",FACE,{"disambiguationData":[OSD([subQ3])]});var subQ7=sQuery(id+"F22.wireOp",EDGE,"E24.bottom");Q0=makeQuery(id+"F24.opChamfer","BLEND_EDGE",EDGE,{"blendedFrom":[makeQuery(id+"F17.boolean.opBoolean","COPY",EDGE,{"disambiguationData":[TD([subQ5])],"derivedFrom":makeQuery(id+"F17.opExtrude","CAP_EDGE",EDGE,{"disambiguationData":[OSD([subQ3])],"isStart":false})}),makeQuery(id+"F23.boolean.opBoolean","COPY",EDGE,{"disambiguationData":[topologyDisambiguationEdgeConnected([makeQuery(id+"F17.boolean.opBoolean","COPY",FACE,{"disambiguationData":[TD([subQ5])],"derivedFrom":subQ6})])],"derivedFrom":makeQuery(id+"F23.opExtrude","CAP_EDGE",EDGE,{"disambiguationData":[OSD([subQ7])],"isStart":false})})],"blendedInto":[]});}
            var Q1;
            {var subQ1=sQuery(id+"F0.wireOp",EDGE,"E0.left");var subQ2=sQuery(id+"F0.wireOp",EDGE,"E0.top");Q1=makeQuery(id+"F17.boolean.opBoolean","SPLIT",EDGE,{"disambiguationData":[TD([makeQuery(id+"F17.opExtrude","SWEPT_FACE",FACE,{"disambiguationData":[OSD([sQuery(id+"F16.wireOp",EDGE,"E21.bottom")])]})])],"derivedFrom":makeQuery(id+"F1.opExtrude","SWEPT_EDGE",EDGE,{"disambiguationData":[OSD([subQ2,subQ1])]})});}
            var Q2;
            {var subQ3=sQuery(id+"F16.wireOp",EDGE,"E21.top");var subQ5=makeQuery(id+"F1.opExtrude","SWEPT_FACE",FACE,{"disambiguationData":[OSD([sQuery(id+"F0.wireOp",EDGE,"E0.left")])]});var subQ6=makeQuery(id+"F17.opExtrude","SWEPT_FACE",FACE,{"disambiguationData":[OSD([subQ3])]});var subQ7=sQuery(id+"F22.wireOp",EDGE,"E24.top");Q2=makeQuery(id+"F24.opChamfer","BLEND_EDGE",EDGE,{"blendedFrom":[makeQuery(id+"F17.boolean.opBoolean","COPY",EDGE,{"disambiguationData":[TD([subQ5])],"derivedFrom":makeQuery(id+"F17.opExtrude","CAP_EDGE",EDGE,{"disambiguationData":[OSD([subQ3])],"isStart":false})}),makeQuery(id+"F23.boolean.opBoolean","COPY",EDGE,{"disambiguationData":[topologyDisambiguationEdgeConnected([makeQuery(id+"F17.boolean.opBoolean","COPY",FACE,{"disambiguationData":[TD([subQ5])],"derivedFrom":subQ6})])],"derivedFrom":makeQuery(id+"F23.opExtrude","CAP_EDGE",EDGE,{"disambiguationData":[OSD([subQ7])],"isStart":false})})],"blendedInto":[]});}
            var Q3;
            Q3=makeQuery(id+"F23.boolean.opBoolean","INTERSECT",EDGE,{"derivedFrom":[makeQuery(id+"F17.boolean.opBoolean","MERGE",FACE,{"derivedFrom":[makeQuery(id+"F13.boolean.opBoolean","COPY",FACE,{"derivedFrom":makeQuery(id+"F13.opExtrude","SWEPT_FACE",FACE,{"disambiguationData":[OSD([sQuery(id+"F12.wireOp",EDGE,"E17.top")])]})}),makeQuery(id+"F17.opExtrude","CAP_FACE",FACE,{"disambiguationData":[OSD([sQuery(id+"F16.wireOp",EDGE,"E21.bottom"),sQuery(id+"F16.wireOp",EDGE,"E21.top"),sQuery(id+"F16.wireOp",EDGE,"E21.left"),sQuery(id+"F16.wireOp",EDGE,"E21.right")])],"isStart":false})]}),makeQuery(id+"F23.opExtrude","CAP_FACE",FACE,{"disambiguationData":[OSD([sQuery(id+"F22.wireOp",EDGE,"E24.bottom"),sQuery(id+"F22.wireOp",EDGE,"E24.top"),sQuery(id+"F22.wireOp",EDGE,"E24.left"),sQuery(id+"F22.wireOp",EDGE,"E24.right")])],"isStart":false})]});
            var Q4;
            {var subQ0=sQuery(id+"F20.wireOp",EDGE,"E23.top");var subQ1=makeQuery(id+"F21.opExtrude","SWEPT_FACE",FACE,{"disambiguationData":[OSD([subQ0])]});var subQ2=sQuery(id+"F22.wireOp",EDGE,"E24.top");Q4=makeQuery(id+"F24.opChamfer","BLEND_EDGE",EDGE,{"blendedFrom":[makeQuery(id+"F21.boolean.opBoolean","COPY",EDGE,{"disambiguationData":[topologyDisambiguationEdgeConnected([makeQuery(id+"F13.boolean.opBoolean","COPY",FACE,{"derivedFrom":makeQuery(id+"F13.opExtrude","SWEPT_FACE",FACE,{"disambiguationData":[OSD([sQuery(id+"F12.wireOp",EDGE,"E20.top")])]})}),makeQuery(id+"F21.opExtrude","CAP_FACE",FACE,{"disambiguationData":[OSD([sQuery(id+"F20.wireOp",EDGE,"E23.bottom"),subQ0,sQuery(id+"F20.wireOp",EDGE,"E23.left"),sQuery(id+"F20.wireOp",EDGE,"E23.right")])],"isStart":false}),subQ1])],"derivedFrom":makeQuery(id+"F21.opExtrude","CAP_EDGE",EDGE,{"disambiguationData":[OSD([subQ0])],"isStart":false})}),makeQuery(id+"F23.boolean.opBoolean","COPY",EDGE,{"disambiguationData":[topologyDisambiguationEdgeConnected([makeQuery(id+"F21.boolean.opBoolean","COPY",FACE,{"derivedFrom":subQ1})])],"derivedFrom":makeQuery(id+"F23.opExtrude","CAP_EDGE",EDGE,{"disambiguationData":[OSD([subQ2])],"isStart":false})})],"blendedInto":[]});}
            var Q5;
            {var subQ0=sQuery(id+"F20.wireOp",EDGE,"E23.bottom");var subQ1=makeQuery(id+"F21.opExtrude","SWEPT_FACE",FACE,{"disambiguationData":[OSD([subQ0])]});var subQ2=sQuery(id+"F22.wireOp",EDGE,"E24.bottom");Q5=makeQuery(id+"F24.opChamfer","BLEND_EDGE",EDGE,{"blendedFrom":[makeQuery(id+"F21.boolean.opBoolean","COPY",EDGE,{"disambiguationData":[topologyDisambiguationEdgeConnected([makeQuery(id+"F13.boolean.opBoolean","COPY",FACE,{"derivedFrom":makeQuery(id+"F13.opExtrude","SWEPT_FACE",FACE,{"disambiguationData":[OSD([sQuery(id+"F12.wireOp",EDGE,"E20.top")])]})}),subQ1,makeQuery(id+"F21.opExtrude","CAP_FACE",FACE,{"disambiguationData":[OSD([subQ0,sQuery(id+"F20.wireOp",EDGE,"E23.top"),sQuery(id+"F20.wireOp",EDGE,"E23.left"),sQuery(id+"F20.wireOp",EDGE,"E23.right")])],"isStart":false})])],"derivedFrom":makeQuery(id+"F21.opExtrude","CAP_EDGE",EDGE,{"disambiguationData":[OSD([subQ0])],"isStart":false})}),makeQuery(id+"F23.boolean.opBoolean","COPY",EDGE,{"disambiguationData":[topologyDisambiguationEdgeConnected([makeQuery(id+"F21.boolean.opBoolean","COPY",FACE,{"derivedFrom":subQ1})])],"derivedFrom":makeQuery(id+"F23.opExtrude","CAP_EDGE",EDGE,{"disambiguationData":[OSD([subQ2])],"isStart":false})})],"blendedInto":[]});}
            var Q6;
            Q6=makeQuery(id+"F23.boolean.opBoolean","INTERSECT",EDGE,{"derivedFrom":[makeQuery(id+"F21.boolean.opBoolean","MERGE",FACE,{"derivedFrom":[makeQuery(id+"F13.boolean.opBoolean","COPY",FACE,{"derivedFrom":makeQuery(id+"F13.opExtrude","SWEPT_FACE",FACE,{"disambiguationData":[OSD([sQuery(id+"F12.wireOp",EDGE,"E20.top")])]})}),makeQuery(id+"F21.opExtrude","CAP_FACE",FACE,{"disambiguationData":[OSD([sQuery(id+"F20.wireOp",EDGE,"E23.bottom"),sQuery(id+"F20.wireOp",EDGE,"E23.top"),sQuery(id+"F20.wireOp",EDGE,"E23.left"),sQuery(id+"F20.wireOp",EDGE,"E23.right")])],"isStart":false})]}),makeQuery(id+"F23.opExtrude","CAP_FACE",FACE,{"disambiguationData":[OSD([sQuery(id+"F22.wireOp",EDGE,"E24.bottom"),sQuery(id+"F22.wireOp",EDGE,"E24.top"),sQuery(id+"F22.wireOp",EDGE,"E24.left"),sQuery(id+"F22.wireOp",EDGE,"E24.right")])],"isStart":false})]});
            var Q7;
            {var subQ0=sQuery(id+"F0.wireOp",EDGE,"E0.bottom");var subQ1=sQuery(id+"F0.wireOp",EDGE,"E0.left");Q7=makeQuery(id+"F21.boolean.opBoolean","SPLIT",EDGE,{"disambiguationData":[TD([makeQuery(id+"F21.opExtrude","SWEPT_FACE",FACE,{"disambiguationData":[OSD([sQuery(id+"F20.wireOp",EDGE,"E23.bottom")])]})])],"derivedFrom":makeQuery(id+"F1.opExtrude","SWEPT_EDGE",EDGE,{"disambiguationData":[OSD([subQ0,subQ1])]})});}
            var Q8;
            {var subQ0=sQuery(id+"F18.wireOp",EDGE,"E22.top");var subQ1=makeQuery(id+"F19.opExtrude","SWEPT_FACE",FACE,{"disambiguationData":[OSD([subQ0])]});var subQ2=sQuery(id+"F20.wireOp",EDGE,"E23.top");Q8=makeQuery(id+"F24.opChamfer","BLEND_EDGE",EDGE,{"blendedFrom":[makeQuery(id+"F19.boolean.opBoolean","COPY",EDGE,{"disambiguationData":[topologyDisambiguationEdgeConnected([makeQuery(id+"F13.boolean.opBoolean","COPY",FACE,{"derivedFrom":makeQuery(id+"F13.opExtrude","SWEPT_FACE",FACE,{"disambiguationData":[OSD([sQuery(id+"F12.wireOp",EDGE,"E18.left")])]})}),makeQuery(id+"F19.opExtrude","CAP_FACE",FACE,{"disambiguationData":[OSD([sQuery(id+"F18.wireOp",EDGE,"E22.bottom"),subQ0,sQuery(id+"F18.wireOp",EDGE,"E22.left"),sQuery(id+"F18.wireOp",EDGE,"E22.right")])],"isStart":false}),subQ1])],"derivedFrom":makeQuery(id+"F19.opExtrude","CAP_EDGE",EDGE,{"disambiguationData":[OSD([subQ0])],"isStart":false})}),makeQuery(id+"F21.boolean.opBoolean","COPY",EDGE,{"disambiguationData":[topologyDisambiguationEdgeConnected([makeQuery(id+"F13.boolean.opBoolean","COPY",FACE,{"derivedFrom":makeQuery(id+"F13.opExtrude","SWEPT_FACE",FACE,{"disambiguationData":[OSD([sQuery(id+"F12.wireOp",EDGE,"E20.top")])]})}),makeQuery(id+"F19.boolean.opBoolean","COPY",FACE,{"derivedFrom":subQ1}),makeQuery(id+"F21.opExtrude","CAP_FACE",FACE,{"disambiguationData":[OSD([sQuery(id+"F20.wireOp",EDGE,"E23.bottom"),subQ2,sQuery(id+"F20.wireOp",EDGE,"E23.left"),sQuery(id+"F20.wireOp",EDGE,"E23.right")])],"isStart":false}),makeQuery(id+"F21.opExtrude","SWEPT_FACE",FACE,{"disambiguationData":[OSD([subQ2])]})])],"derivedFrom":makeQuery(id+"F21.opExtrude","CAP_EDGE",EDGE,{"disambiguationData":[OSD([subQ2])],"isStart":false})})],"blendedInto":[]});}
            var Q9;
            Q9=makeQuery(id+"F21.boolean.opBoolean","INTERSECT",EDGE,{"derivedFrom":[makeQuery(id+"F19.boolean.opBoolean","MERGE",FACE,{"derivedFrom":[makeQuery(id+"F13.boolean.opBoolean","COPY",FACE,{"derivedFrom":makeQuery(id+"F13.opExtrude","SWEPT_FACE",FACE,{"disambiguationData":[OSD([sQuery(id+"F12.wireOp",EDGE,"E18.left")])]})}),makeQuery(id+"F19.opExtrude","CAP_FACE",FACE,{"disambiguationData":[OSD([sQuery(id+"F18.wireOp",EDGE,"E22.bottom"),sQuery(id+"F18.wireOp",EDGE,"E22.top"),sQuery(id+"F18.wireOp",EDGE,"E22.left"),sQuery(id+"F18.wireOp",EDGE,"E22.right")])],"isStart":false})]}),makeQuery(id+"F21.opExtrude","CAP_FACE",FACE,{"disambiguationData":[OSD([sQuery(id+"F20.wireOp",EDGE,"E23.bottom"),sQuery(id+"F20.wireOp",EDGE,"E23.top"),sQuery(id+"F20.wireOp",EDGE,"E23.left"),sQuery(id+"F20.wireOp",EDGE,"E23.right")])],"isStart":false})]});
            var Q10;
            {var subQ0=sQuery(id+"F18.wireOp",EDGE,"E22.bottom");var subQ1=makeQuery(id+"F19.opExtrude","SWEPT_FACE",FACE,{"disambiguationData":[OSD([subQ0])]});var subQ2=sQuery(id+"F20.wireOp",EDGE,"E23.bottom");Q10=makeQuery(id+"F24.opChamfer","BLEND_EDGE",EDGE,{"blendedFrom":[makeQuery(id+"F19.boolean.opBoolean","COPY",EDGE,{"disambiguationData":[topologyDisambiguationEdgeConnected([makeQuery(id+"F13.boolean.opBoolean","COPY",FACE,{"derivedFrom":makeQuery(id+"F13.opExtrude","SWEPT_FACE",FACE,{"disambiguationData":[OSD([sQuery(id+"F12.wireOp",EDGE,"E18.left")])]})}),subQ1,makeQuery(id+"F19.opExtrude","CAP_FACE",FACE,{"disambiguationData":[OSD([subQ0,sQuery(id+"F18.wireOp",EDGE,"E22.top"),sQuery(id+"F18.wireOp",EDGE,"E22.left"),sQuery(id+"F18.wireOp",EDGE,"E22.right")])],"isStart":false})])],"derivedFrom":makeQuery(id+"F19.opExtrude","CAP_EDGE",EDGE,{"disambiguationData":[OSD([subQ0])],"isStart":false})}),makeQuery(id+"F21.boolean.opBoolean","COPY",EDGE,{"disambiguationData":[topologyDisambiguationEdgeConnected([makeQuery(id+"F13.boolean.opBoolean","COPY",FACE,{"derivedFrom":makeQuery(id+"F13.opExtrude","SWEPT_FACE",FACE,{"disambiguationData":[OSD([sQuery(id+"F12.wireOp",EDGE,"E20.top")])]})}),makeQuery(id+"F19.boolean.opBoolean","COPY",FACE,{"derivedFrom":subQ1}),makeQuery(id+"F21.opExtrude","SWEPT_FACE",FACE,{"disambiguationData":[OSD([subQ2])]}),makeQuery(id+"F21.opExtrude","CAP_FACE",FACE,{"disambiguationData":[OSD([subQ2,sQuery(id+"F20.wireOp",EDGE,"E23.top"),sQuery(id+"F20.wireOp",EDGE,"E23.left"),sQuery(id+"F20.wireOp",EDGE,"E23.right")])],"isStart":false})])],"derivedFrom":makeQuery(id+"F21.opExtrude","CAP_EDGE",EDGE,{"disambiguationData":[OSD([subQ2])],"isStart":false})})],"blendedInto":[]});}
            var Q11;
            {var subQ0=sQuery(id+"F0.wireOp",EDGE,"E0.bottom");var subQ1=sQuery(id+"F0.wireOp",EDGE,"E0.right");Q11=makeQuery(id+"F19.boolean.opBoolean","SPLIT",EDGE,{"disambiguationData":[TD([makeQuery(id+"F19.opExtrude","SWEPT_FACE",FACE,{"disambiguationData":[OSD([sQuery(id+"F18.wireOp",EDGE,"E22.bottom")])]})])],"derivedFrom":makeQuery(id+"F1.opExtrude","SWEPT_EDGE",EDGE,{"disambiguationData":[OSD([subQ0,subQ1])]})});}
            var Q12;
            {var subQ3=sQuery(id+"F16.wireOp",EDGE,"E21.top");var subQ5=makeQuery(id+"F1.opExtrude","SWEPT_FACE",FACE,{"disambiguationData":[OSD([sQuery(id+"F0.wireOp",EDGE,"E0.right")])]});var subQ6=makeQuery(id+"F17.opExtrude","SWEPT_FACE",FACE,{"disambiguationData":[OSD([subQ3])]});var subQ7=sQuery(id+"F18.wireOp",EDGE,"E22.top");Q12=makeQuery(id+"F24.opChamfer","BLEND_EDGE",EDGE,{"blendedFrom":[makeQuery(id+"F17.boolean.opBoolean","COPY",EDGE,{"disambiguationData":[TD([subQ5])],"derivedFrom":makeQuery(id+"F17.opExtrude","CAP_EDGE",EDGE,{"disambiguationData":[OSD([subQ3])],"isStart":false})}),makeQuery(id+"F19.boolean.opBoolean","COPY",EDGE,{"disambiguationData":[topologyDisambiguationEdgeConnected([makeQuery(id+"F13.boolean.opBoolean","COPY",FACE,{"derivedFrom":makeQuery(id+"F13.opExtrude","SWEPT_FACE",FACE,{"disambiguationData":[OSD([sQuery(id+"F12.wireOp",EDGE,"E18.left")])]})}),makeQuery(id+"F17.boolean.opBoolean","COPY",FACE,{"disambiguationData":[TD([subQ5])],"derivedFrom":subQ6}),makeQuery(id+"F19.opExtrude","CAP_FACE",FACE,{"disambiguationData":[OSD([sQuery(id+"F18.wireOp",EDGE,"E22.bottom"),subQ7,sQuery(id+"F18.wireOp",EDGE,"E22.left"),sQuery(id+"F18.wireOp",EDGE,"E22.right")])],"isStart":false}),makeQuery(id+"F19.opExtrude","SWEPT_FACE",FACE,{"disambiguationData":[OSD([subQ7])]})])],"derivedFrom":makeQuery(id+"F19.opExtrude","CAP_EDGE",EDGE,{"disambiguationData":[OSD([subQ7])],"isStart":false})})],"blendedInto":[]});}
            var Q13;
            {var subQ3=sQuery(id+"F16.wireOp",EDGE,"E21.bottom");var subQ5=makeQuery(id+"F1.opExtrude","SWEPT_FACE",FACE,{"disambiguationData":[OSD([sQuery(id+"F0.wireOp",EDGE,"E0.right")])]});var subQ6=makeQuery(id+"F17.opExtrude","SWEPT_FACE",FACE,{"disambiguationData":[OSD([subQ3])]});var subQ7=sQuery(id+"F18.wireOp",EDGE,"E22.bottom");Q13=makeQuery(id+"F24.opChamfer","BLEND_EDGE",EDGE,{"blendedFrom":[makeQuery(id+"F17.boolean.opBoolean","COPY",EDGE,{"disambiguationData":[TD([subQ5])],"derivedFrom":makeQuery(id+"F17.opExtrude","CAP_EDGE",EDGE,{"disambiguationData":[OSD([subQ3])],"isStart":false})}),makeQuery(id+"F19.boolean.opBoolean","COPY",EDGE,{"disambiguationData":[topologyDisambiguationEdgeConnected([makeQuery(id+"F13.boolean.opBoolean","COPY",FACE,{"derivedFrom":makeQuery(id+"F13.opExtrude","SWEPT_FACE",FACE,{"disambiguationData":[OSD([sQuery(id+"F12.wireOp",EDGE,"E18.left")])]})}),makeQuery(id+"F17.boolean.opBoolean","COPY",FACE,{"disambiguationData":[TD([subQ5])],"derivedFrom":subQ6}),makeQuery(id+"F19.opExtrude","SWEPT_FACE",FACE,{"disambiguationData":[OSD([subQ7])]}),makeQuery(id+"F19.opExtrude","CAP_FACE",FACE,{"disambiguationData":[OSD([subQ7,sQuery(id+"F18.wireOp",EDGE,"E22.top"),sQuery(id+"F18.wireOp",EDGE,"E22.left"),sQuery(id+"F18.wireOp",EDGE,"E22.right")])],"isStart":false})])],"derivedFrom":makeQuery(id+"F19.opExtrude","CAP_EDGE",EDGE,{"disambiguationData":[OSD([subQ7])],"isStart":false})})],"blendedInto":[]});}
            var Q14;
            {var subQ1=sQuery(id+"F0.wireOp",EDGE,"E0.right");var subQ2=sQuery(id+"F0.wireOp",EDGE,"E0.top");Q14=makeQuery(id+"F17.boolean.opBoolean","SPLIT",EDGE,{"disambiguationData":[TD([makeQuery(id+"F17.opExtrude","SWEPT_FACE",FACE,{"disambiguationData":[OSD([sQuery(id+"F16.wireOp",EDGE,"E21.bottom")])]})])],"derivedFrom":makeQuery(id+"F1.opExtrude","SWEPT_EDGE",EDGE,{"disambiguationData":[OSD([subQ2,subQ1])]})});}
            var Q15;
            Q15=makeQuery(id+"F19.boolean.opBoolean","INTERSECT",EDGE,{"derivedFrom":[makeQuery(id+"F17.boolean.opBoolean","MERGE",FACE,{"derivedFrom":[makeQuery(id+"F13.boolean.opBoolean","COPY",FACE,{"derivedFrom":makeQuery(id+"F13.opExtrude","SWEPT_FACE",FACE,{"disambiguationData":[OSD([sQuery(id+"F12.wireOp",EDGE,"E17.top")])]})}),makeQuery(id+"F17.opExtrude","CAP_FACE",FACE,{"disambiguationData":[OSD([sQuery(id+"F16.wireOp",EDGE,"E21.bottom"),sQuery(id+"F16.wireOp",EDGE,"E21.top"),sQuery(id+"F16.wireOp",EDGE,"E21.left"),sQuery(id+"F16.wireOp",EDGE,"E21.right")])],"isStart":false})]}),makeQuery(id+"F19.opExtrude","CAP_FACE",FACE,{"disambiguationData":[OSD([sQuery(id+"F18.wireOp",EDGE,"E22.bottom"),sQuery(id+"F18.wireOp",EDGE,"E22.top"),sQuery(id+"F18.wireOp",EDGE,"E22.left"),sQuery(id+"F18.wireOp",EDGE,"E22.right")])],"isStart":false})]});
            fillet(context, id + "F25", {"entities" : qUnion([Q0, Q1, Q2, Q3, Q4, Q5, Q6, Q7, Q8, Q9, Q10, Q11, Q12, Q13, Q14, Q15]), "radius" : 3 * mm, "tangentPropagation" : true, "allowEdgeOverflow" : false});
        }
        {
            var Q0;
            Q0=makeQuery(id+"F1.opExtrude","CAP_FACE",FACE,{"disambiguationData":[OSD([sQuery(id+"F0.wireOp",EDGE,"E0.bottom"),sQuery(id+"F0.wireOp",EDGE,"E0.top"),sQuery(id+"F0.wireOp",EDGE,"E0.left"),sQuery(id+"F0.wireOp",EDGE,"E0.right"),sQuery(id+"F0.wireOp",EDGE,"E1"),sQuery(id+"F0.wireOp",EDGE,"E2.bottom")])],"isStart":true});
            var sketch = newSketch(context, id + "F26", { "sketchPlane" : qUnion([Q0])});
            skLineSegment(sketch, "E25.bottom", {"start": v(-33, 50) * mm, "end": v(-50, 50) * mm});
            skLineSegment(sketch, "E25.top", {"start": v(-33, 33) * mm, "end": v(-50, 33) * mm});
            skLineSegment(sketch, "E25.left", {"start": v(-33, 50) * mm, "end": v(-33, 33) * mm});
            skLineSegment(sketch, "E25.right", {"start": v(-50, 50) * mm, "end": v(-50, 33) * mm});
            skLineSegment(sketch, "E26.bottom", {"start": v(50, 50) * mm, "end": v(33, 50) * mm});
            skLineSegment(sketch, "E26.top", {"start": v(50, 33) * mm, "end": v(33, 33) * mm});
            skLineSegment(sketch, "E26.left", {"start": v(50, 50) * mm, "end": v(50, 33) * mm});
            skLineSegment(sketch, "E26.right", {"start": v(33, 50) * mm, "end": v(33, 33) * mm});
            skLineSegment(sketch, "E27.bottom", {"start": v(50, -33) * mm, "end": v(33, -33) * mm});
            skLineSegment(sketch, "E27.top", {"start": v(50, -50) * mm, "end": v(33, -50) * mm});
            skLineSegment(sketch, "E27.left", {"start": v(50, -33) * mm, "end": v(50, -50) * mm});
            skLineSegment(sketch, "E27.right", {"start": v(33, -33) * mm, "end": v(33, -50) * mm});
            skLineSegment(sketch, "E28.bottom", {"start": v(-33, -33) * mm, "end": v(-50, -33) * mm});
            skLineSegment(sketch, "E28.top", {"start": v(-33, -50) * mm, "end": v(-50, -50) * mm});
            skLineSegment(sketch, "E28.left", {"start": v(-33, -33) * mm, "end": v(-33, -50) * mm});
            skLineSegment(sketch, "E28.right", {"start": v(-50, -33) * mm, "end": v(-50, -50) * mm});
            skSolve(sketch);
        }
        {
            var Q0;
            Q0=qSketchRegion(id+"F26",true);
            extrude(context, id + "F27", {"entities" : qUnion([Q0]), "operationType" : NewBodyOperationType.REMOVE, "oppositeDirection" : true, "depth" : 8 * mm});
        }
        {
            var Q0;
            Q0=makeQuery(id+"F27.boolean.opBoolean","COPY",FACE,{"derivedFrom":makeQuery(id+"F27.opExtrude","CAP_FACE",FACE,{"disambiguationData":[OSD([sQuery(id+"F26.wireOp",EDGE,"E25.bottom"),sQuery(id+"F26.wireOp",EDGE,"E25.top"),sQuery(id+"F26.wireOp",EDGE,"E25.left"),sQuery(id+"F26.wireOp",EDGE,"E25.right")])],"isStart":false})});
            var sketch = newSketch(context, id + "F28", { "sketchPlane" : qUnion([Q0])});
            skLineSegment(sketch, "E29.bottom", {"start": v(-33, 42) * mm, "end": v(-42, 42) * mm});
            skLineSegment(sketch, "E29.top", {"start": v(-33, 33) * mm, "end": v(-42, 33) * mm});
            skLineSegment(sketch, "E29.left", {"start": v(-33, 42) * mm, "end": v(-33, 33) * mm});
            skLineSegment(sketch, "E29.right", {"start": v(-42, 42) * mm, "end": v(-42, 33) * mm});
            skSolve(sketch);
        }
        {
            var Q0;
            Q0=qSketchRegion(id+"F28",true);
            extrude(context, id + "F29", {"entities" : qUnion([Q0]), "operationType" : NewBodyOperationType.REMOVE, "oppositeDirection" : true, "depth" : 10 * mm});
        }
        {
            var Q0;
            Q0=makeQuery(id+"F27.boolean.opBoolean","COPY",FACE,{"derivedFrom":makeQuery(id+"F27.opExtrude","CAP_FACE",FACE,{"disambiguationData":[OSD([sQuery(id+"F26.wireOp",EDGE,"E26.bottom"),sQuery(id+"F26.wireOp",EDGE,"E26.top"),sQuery(id+"F26.wireOp",EDGE,"E26.left"),sQuery(id+"F26.wireOp",EDGE,"E26.right")])],"isStart":false})});
            var sketch = newSketch(context, id + "F30", { "sketchPlane" : qUnion([Q0])});
            skLineSegment(sketch, "E30.bottom", {"start": v(42, 42) * mm, "end": v(33, 42) * mm});
            skLineSegment(sketch, "E30.top", {"start": v(42, 33) * mm, "end": v(33, 33) * mm});
            skLineSegment(sketch, "E30.left", {"start": v(42, 42) * mm, "end": v(42, 33) * mm});
            skLineSegment(sketch, "E30.right", {"start": v(33, 42) * mm, "end": v(33, 33) * mm});
            skSolve(sketch);
        }
        {
            var Q0;
            Q0=qSketchRegion(id+"F30",true);
            extrude(context, id + "F31", {"entities" : qUnion([Q0]), "operationType" : NewBodyOperationType.REMOVE, "oppositeDirection" : true, "depth" : 10 * mm});
        }
        {
            var Q0;
            Q0=makeQuery(id+"F27.boolean.opBoolean","COPY",FACE,{"derivedFrom":makeQuery(id+"F27.opExtrude","CAP_FACE",FACE,{"disambiguationData":[OSD([sQuery(id+"F26.wireOp",EDGE,"E28.bottom"),sQuery(id+"F26.wireOp",EDGE,"E28.top"),sQuery(id+"F26.wireOp",EDGE,"E28.left"),sQuery(id+"F26.wireOp",EDGE,"E28.right")])],"isStart":false})});
            var sketch = newSketch(context, id + "F32", { "sketchPlane" : qUnion([Q0])});
            skLineSegment(sketch, "E31.bottom", {"start": v(-33, -33) * mm, "end": v(-42, -33) * mm});
            skLineSegment(sketch, "E31.top", {"start": v(-33, -42) * mm, "end": v(-42, -42) * mm});
            skLineSegment(sketch, "E31.left", {"start": v(-33, -33) * mm, "end": v(-33, -42) * mm});
            skLineSegment(sketch, "E31.right", {"start": v(-42, -33) * mm, "end": v(-42, -42) * mm});
            skSolve(sketch);
        }
        {
            var Q0;
            Q0=qSketchRegion(id+"F32",true);
            extrude(context, id + "F33", {"entities" : qUnion([Q0]), "operationType" : NewBodyOperationType.REMOVE, "oppositeDirection" : true, "depth" : 10 * mm});
        }
        {
            var Q0;
            Q0=makeQuery(id+"F27.boolean.opBoolean","COPY",FACE,{"derivedFrom":makeQuery(id+"F27.opExtrude","CAP_FACE",FACE,{"disambiguationData":[OSD([sQuery(id+"F26.wireOp",EDGE,"E27.bottom"),sQuery(id+"F26.wireOp",EDGE,"E27.top"),sQuery(id+"F26.wireOp",EDGE,"E27.left"),sQuery(id+"F26.wireOp",EDGE,"E27.right")])],"isStart":false})});
            var sketch = newSketch(context, id + "F34", { "sketchPlane" : qUnion([Q0])});
            skLineSegment(sketch, "E32.bottom", {"start": v(42, -33) * mm, "end": v(33, -33) * mm});
            skLineSegment(sketch, "E32.top", {"start": v(42, -42) * mm, "end": v(33, -42) * mm});
            skLineSegment(sketch, "E32.left", {"start": v(42, -33) * mm, "end": v(42, -42) * mm});
            skLineSegment(sketch, "E32.right", {"start": v(33, -33) * mm, "end": v(33, -42) * mm});
            skSolve(sketch);
        }
        {
            var Q0;
            Q0=qSketchRegion(id+"F34",true);
            extrude(context, id + "F35", {"entities" : qUnion([Q0]), "operationType" : NewBodyOperationType.REMOVE, "oppositeDirection" : true, "depth" : 10 * mm});
        }
        {
            var Q0;
            Q0=makeQuery(id+"F29.boolean.opBoolean","MERGE",EDGE,{"derivedFrom":[makeQuery(id+"F27.boolean.opBoolean","COPY",EDGE,{"derivedFrom":makeQuery(id+"F27.opExtrude","SWEPT_EDGE",EDGE,{"disambiguationData":[OSD([sQuery(id+"F26.wireOp",EDGE,"E25.top"),sQuery(id+"F26.wireOp",EDGE,"E25.left")])]})}),makeQuery(id+"F29.opExtrude","SWEPT_EDGE",EDGE,{"disambiguationData":[OSD([sQuery(id+"F28.wireOp",EDGE,"E29.top"),sQuery(id+"F28.wireOp",EDGE,"E29.left")])]})]});
            var Q1;
            Q1=makeQuery(id+"F29.boolean.opBoolean","COPY",EDGE,{"derivedFrom":makeQuery(id+"F29.opExtrude","SWEPT_EDGE",EDGE,{"disambiguationData":[OSD([sQuery(id+"F26.wireOp",EDGE,"E25.top"),sQuery(id+"F28.wireOp",EDGE,"E29.top"),sQuery(id+"F28.wireOp",EDGE,"E29.right")])]})});
            var Q2;
            Q2=makeQuery(id+"F31.boolean.opBoolean","MERGE",EDGE,{"derivedFrom":[makeQuery(id+"F27.boolean.opBoolean","COPY",EDGE,{"derivedFrom":makeQuery(id+"F27.opExtrude","SWEPT_EDGE",EDGE,{"disambiguationData":[OSD([sQuery(id+"F26.wireOp",EDGE,"E26.top"),sQuery(id+"F26.wireOp",EDGE,"E26.right")])]})}),makeQuery(id+"F31.opExtrude","SWEPT_EDGE",EDGE,{"disambiguationData":[OSD([sQuery(id+"F30.wireOp",EDGE,"E30.top"),sQuery(id+"F30.wireOp",EDGE,"E30.right")])]})]});
            var Q3;
            Q3=makeQuery(id+"F31.boolean.opBoolean","COPY",EDGE,{"derivedFrom":makeQuery(id+"F31.opExtrude","SWEPT_EDGE",EDGE,{"disambiguationData":[OSD([sQuery(id+"F26.wireOp",EDGE,"E26.top"),sQuery(id+"F30.wireOp",EDGE,"E30.top"),sQuery(id+"F30.wireOp",EDGE,"E30.left")])]})});
            var Q4;
            Q4=makeQuery(id+"F31.boolean.opBoolean","COPY",EDGE,{"derivedFrom":makeQuery(id+"F31.opExtrude","SWEPT_EDGE",EDGE,{"disambiguationData":[OSD([sQuery(id+"F26.wireOp",EDGE,"E26.right"),sQuery(id+"F30.wireOp",EDGE,"E30.bottom"),sQuery(id+"F30.wireOp",EDGE,"E30.right")])]})});
            var Q5;
            Q5=makeQuery(id+"F31.boolean.opBoolean","COPY",EDGE,{"derivedFrom":makeQuery(id+"F31.opExtrude","SWEPT_EDGE",EDGE,{"disambiguationData":[OSD([sQuery(id+"F30.wireOp",EDGE,"E30.bottom"),sQuery(id+"F30.wireOp",EDGE,"E30.left")])]})});
            var Q6;
            Q6=makeQuery(id+"F29.boolean.opBoolean","COPY",EDGE,{"derivedFrom":makeQuery(id+"F29.opExtrude","SWEPT_EDGE",EDGE,{"disambiguationData":[OSD([sQuery(id+"F28.wireOp",EDGE,"E29.bottom"),sQuery(id+"F28.wireOp",EDGE,"E29.right")])]})});
            var Q7;
            Q7=makeQuery(id+"F29.boolean.opBoolean","COPY",EDGE,{"derivedFrom":makeQuery(id+"F29.opExtrude","SWEPT_EDGE",EDGE,{"disambiguationData":[OSD([sQuery(id+"F26.wireOp",EDGE,"E25.left"),sQuery(id+"F28.wireOp",EDGE,"E29.bottom"),sQuery(id+"F28.wireOp",EDGE,"E29.left")])]})});
            var Q8;
            Q8=makeQuery(id+"F35.boolean.opBoolean","MERGE",EDGE,{"derivedFrom":[makeQuery(id+"F27.boolean.opBoolean","COPY",EDGE,{"derivedFrom":makeQuery(id+"F27.opExtrude","SWEPT_EDGE",EDGE,{"disambiguationData":[OSD([sQuery(id+"F26.wireOp",EDGE,"E27.bottom"),sQuery(id+"F26.wireOp",EDGE,"E27.right")])]})}),makeQuery(id+"F35.opExtrude","SWEPT_EDGE",EDGE,{"disambiguationData":[OSD([sQuery(id+"F34.wireOp",EDGE,"E32.bottom"),sQuery(id+"F34.wireOp",EDGE,"E32.right")])]})]});
            var Q9;
            Q9=makeQuery(id+"F35.boolean.opBoolean","COPY",EDGE,{"derivedFrom":makeQuery(id+"F35.opExtrude","SWEPT_EDGE",EDGE,{"disambiguationData":[OSD([sQuery(id+"F26.wireOp",EDGE,"E27.bottom"),sQuery(id+"F34.wireOp",EDGE,"E32.bottom"),sQuery(id+"F34.wireOp",EDGE,"E32.left")])]})});
            var Q10;
            Q10=makeQuery(id+"F33.boolean.opBoolean","COPY",EDGE,{"derivedFrom":makeQuery(id+"F33.opExtrude","SWEPT_EDGE",EDGE,{"disambiguationData":[OSD([sQuery(id+"F26.wireOp",EDGE,"E28.left"),sQuery(id+"F32.wireOp",EDGE,"E31.top"),sQuery(id+"F32.wireOp",EDGE,"E31.left")])]})});
            var Q11;
            Q11=makeQuery(id+"F35.boolean.opBoolean","COPY",EDGE,{"derivedFrom":makeQuery(id+"F35.opExtrude","SWEPT_EDGE",EDGE,{"disambiguationData":[OSD([sQuery(id+"F34.wireOp",EDGE,"E32.top"),sQuery(id+"F34.wireOp",EDGE,"E32.left")])]})});
            var Q12;
            Q12=makeQuery(id+"F35.boolean.opBoolean","COPY",EDGE,{"derivedFrom":makeQuery(id+"F35.opExtrude","SWEPT_EDGE",EDGE,{"disambiguationData":[OSD([sQuery(id+"F26.wireOp",EDGE,"E27.right"),sQuery(id+"F34.wireOp",EDGE,"E32.top"),sQuery(id+"F34.wireOp",EDGE,"E32.right")])]})});
            var Q13;
            Q13=makeQuery(id+"F33.boolean.opBoolean","MERGE",EDGE,{"derivedFrom":[makeQuery(id+"F27.boolean.opBoolean","COPY",EDGE,{"derivedFrom":makeQuery(id+"F27.opExtrude","SWEPT_EDGE",EDGE,{"disambiguationData":[OSD([sQuery(id+"F26.wireOp",EDGE,"E28.bottom"),sQuery(id+"F26.wireOp",EDGE,"E28.left")])]})}),makeQuery(id+"F33.opExtrude","SWEPT_EDGE",EDGE,{"disambiguationData":[OSD([sQuery(id+"F32.wireOp",EDGE,"E31.bottom"),sQuery(id+"F32.wireOp",EDGE,"E31.left")])]})]});
            var Q14;
            Q14=makeQuery(id+"F33.boolean.opBoolean","COPY",EDGE,{"derivedFrom":makeQuery(id+"F33.opExtrude","SWEPT_EDGE",EDGE,{"disambiguationData":[OSD([sQuery(id+"F26.wireOp",EDGE,"E28.bottom"),sQuery(id+"F32.wireOp",EDGE,"E31.bottom"),sQuery(id+"F32.wireOp",EDGE,"E31.right")])]})});
            var Q15;
            Q15=makeQuery(id+"F33.boolean.opBoolean","COPY",EDGE,{"derivedFrom":makeQuery(id+"F33.opExtrude","SWEPT_EDGE",EDGE,{"disambiguationData":[OSD([sQuery(id+"F32.wireOp",EDGE,"E31.top"),sQuery(id+"F32.wireOp",EDGE,"E31.right")])]})});
            fillet(context, id + "F36", {"entities" : qUnion([Q0, Q1, Q2, Q3, Q4, Q5, Q6, Q7, Q8, Q9, Q10, Q11, Q12, Q13, Q14, Q15]), "radius" : 1 * mm, "tangentPropagation" : true, "allowEdgeOverflow" : false});
        }
        {
            var Q0;
            Q0=makeQuery(id+"F1.opExtrude","CAP_FACE",FACE,{"disambiguationData":[OSD([sQuery(id+"F0.wireOp",EDGE,"E0.bottom"),sQuery(id+"F0.wireOp",EDGE,"E0.top"),sQuery(id+"F0.wireOp",EDGE,"E0.left"),sQuery(id+"F0.wireOp",EDGE,"E0.right"),sQuery(id+"F0.wireOp",EDGE,"E1"),sQuery(id+"F0.wireOp",EDGE,"E2.bottom")])],"isStart":true});
            var sketch = newSketch(context, id + "F37", { "sketchPlane" : qUnion([Q0])});
            skLineSegment(sketch, "E33.bottom", {"start": v(-10, 30) * mm, "end": v(-30, 30) * mm});
            skLineSegment(sketch, "E33.top", {"start": v(-10, 10) * mm, "end": v(-30, 10) * mm});
            skLineSegment(sketch, "E33.left", {"start": v(-10, 30) * mm, "end": v(-10, 10) * mm});
            skLineSegment(sketch, "E33.right", {"start": v(-30, 30) * mm, "end": v(-30, 10) * mm});
            skLineSegment(sketch, "E34.bottom", {"start": v(30, 30) * mm, "end": v(10, 30) * mm});
            skLineSegment(sketch, "E34.top", {"start": v(30, 10) * mm, "end": v(10, 10) * mm});
            skLineSegment(sketch, "E34.left", {"start": v(30, 30) * mm, "end": v(30, 10) * mm});
            skLineSegment(sketch, "E34.right", {"start": v(10, 30) * mm, "end": v(10, 10) * mm});
            skLineSegment(sketch, "E35.bottom", {"start": v(30, -10) * mm, "end": v(10, -10) * mm});
            skLineSegment(sketch, "E35.top", {"start": v(30, -30) * mm, "end": v(10, -30) * mm});
            skLineSegment(sketch, "E35.left", {"start": v(30, -10) * mm, "end": v(30, -30) * mm});
            skLineSegment(sketch, "E35.right", {"start": v(10, -10) * mm, "end": v(10, -30) * mm});
            skLineSegment(sketch, "E36.bottom", {"start": v(-10, -10) * mm, "end": v(-30, -10) * mm});
            skLineSegment(sketch, "E36.top", {"start": v(-10, -30) * mm, "end": v(-30, -30) * mm});
            skLineSegment(sketch, "E36.left", {"start": v(-10, -10) * mm, "end": v(-10, -30) * mm});
            skLineSegment(sketch, "E36.right", {"start": v(-30, -10) * mm, "end": v(-30, -30) * mm});
            skSolve(sketch);
        }
        {
            var Q0;
            Q0=qSketchRegion(id+"F37",true);
            extrude(context, id + "F38", {"entities" : qUnion([Q0]), "operationType" : NewBodyOperationType.REMOVE, "oppositeDirection" : true, "depth" : 18 * mm});
        }
        {
            var Q0;
            Q0=makeQuery(id+"F38.boolean.opBoolean","COPY",FACE,{"derivedFrom":makeQuery(id+"F38.opExtrude","CAP_FACE",FACE,{"disambiguationData":[OSD([sQuery(id+"F37.wireOp",EDGE,"E33.bottom"),sQuery(id+"F37.wireOp",EDGE,"E33.top"),sQuery(id+"F37.wireOp",EDGE,"E33.left"),sQuery(id+"F37.wireOp",EDGE,"E33.right")])],"isStart":false})});
            var sketch = newSketch(context, id + "F39", { "sketchPlane" : qUnion([Q0])});
            skLineSegment(sketch, "E37.bottom", {"start": v(-14, 14) * mm, "end": v(-30, 14) * mm});
            skLineSegment(sketch, "E37.top", {"start": v(-14, 30) * mm, "end": v(-30, 30) * mm});
            skLineSegment(sketch, "E37.left", {"start": v(-14, 14) * mm, "end": v(-14, 30) * mm});
            skLineSegment(sketch, "E37.right", {"start": v(-30, 14) * mm, "end": v(-30, 30) * mm});
            skSolve(sketch);
        }
        {
            var Q0;
            Q0=qSketchRegion(id+"F39",true);
            extrude(context, id + "F40", {"entities" : qUnion([Q0]), "operationType" : NewBodyOperationType.ADD, "depth" : 6 * mm});
        }
        {
            var Q0;
            Q0=makeQuery(id+"F40.opExtrude","CAP_FACE",FACE,{"disambiguationData":[OSD([sQuery(id+"F39.wireOp",EDGE,"E37.bottom"),sQuery(id+"F39.wireOp",EDGE,"E37.top"),sQuery(id+"F39.wireOp",EDGE,"E37.left"),sQuery(id+"F39.wireOp",EDGE,"E37.right")])],"isStart":false});
            var sketch = newSketch(context, id + "F41", { "sketchPlane" : qUnion([Q0])});
            skCircle(sketch, "E38.cCircle", {"center": v(-22.5, 22.5) * mm, "radius": 4 * mm, "construction": true});
            skLineSegment(sketch, "E38.0", {"start": v(-17.9, 22.2) * mm, "end": v(-20.45, 18.36) * mm});
            skLineSegment(sketch, "E38.1", {"start": v(-20.45, 18.36) * mm, "end": v(-25.06, 18.65) * mm});
            skLineSegment(sketch, "E38.2", {"start": v(-25.06, 18.65) * mm, "end": v(-27.1, 22.8) * mm});
            skLineSegment(sketch, "E38.3", {"start": v(-27.1, 22.8) * mm, "end": v(-24.55, 26.64) * mm});
            skLineSegment(sketch, "E38.4", {"start": v(-24.55, 26.64) * mm, "end": v(-19.94, 26.35) * mm});
            skLineSegment(sketch, "E38.5", {"start": v(-19.94, 26.35) * mm, "end": v(-17.9, 22.2) * mm});
            skPoint(sketch, "E38.0.midPoint", {"position": v(-19.17, 20.29) * mm});
            skSolve(sketch);
        }
        {
            var Q0;
            Q0=qSketchRegion(id+"F41",true);
            extrude(context, id + "F42", {"entities" : qUnion([Q0]), "operationType" : NewBodyOperationType.REMOVE, "oppositeDirection" : true, "depth" : 7 * mm});
        }
        {
            var Q0;
            Q0=makeQuery(id+"F38.boolean.opBoolean","COPY",FACE,{"derivedFrom":makeQuery(id+"F38.opExtrude","CAP_FACE",FACE,{"disambiguationData":[OSD([sQuery(id+"F37.wireOp",EDGE,"E34.bottom"),sQuery(id+"F37.wireOp",EDGE,"E34.top"),sQuery(id+"F37.wireOp",EDGE,"E34.left"),sQuery(id+"F37.wireOp",EDGE,"E34.right")])],"isStart":false})});
            var sketch = newSketch(context, id + "F43", { "sketchPlane" : qUnion([Q0])});
            skLineSegment(sketch, "E39.bottom", {"start": v(30, 30) * mm, "end": v(14, 30) * mm});
            skLineSegment(sketch, "E39.top", {"start": v(30, 14) * mm, "end": v(14, 14) * mm});
            skLineSegment(sketch, "E39.left", {"start": v(30, 30) * mm, "end": v(30, 14) * mm});
            skLineSegment(sketch, "E39.right", {"start": v(14, 30) * mm, "end": v(14, 14) * mm});
            skSolve(sketch);
        }
        {
            var Q0;
            Q0=qSketchRegion(id+"F43",true);
            extrude(context, id + "F44", {"entities" : qUnion([Q0]), "operationType" : NewBodyOperationType.ADD, "depth" : 6 * mm});
        }
        {
            var Q0;
            Q0=makeQuery(id+"F38.boolean.opBoolean","COPY",FACE,{"derivedFrom":makeQuery(id+"F38.opExtrude","CAP_FACE",FACE,{"disambiguationData":[OSD([sQuery(id+"F37.wireOp",EDGE,"E36.bottom"),sQuery(id+"F37.wireOp",EDGE,"E36.top"),sQuery(id+"F37.wireOp",EDGE,"E36.left"),sQuery(id+"F37.wireOp",EDGE,"E36.right")])],"isStart":false})});
            var sketch = newSketch(context, id + "F45", { "sketchPlane" : qUnion([Q0])});
            skLineSegment(sketch, "E40.bottom", {"start": v(-14, -14) * mm, "end": v(-30, -14) * mm});
            skLineSegment(sketch, "E40.top", {"start": v(-14, -30) * mm, "end": v(-30, -30) * mm});
            skLineSegment(sketch, "E40.left", {"start": v(-14, -14) * mm, "end": v(-14, -30) * mm});
            skLineSegment(sketch, "E40.right", {"start": v(-30, -14) * mm, "end": v(-30, -30) * mm});
            skSolve(sketch);
        }
        {
            var Q0;
            Q0=qSketchRegion(id+"F45",true);
            extrude(context, id + "F46", {"entities" : qUnion([Q0]), "operationType" : NewBodyOperationType.ADD, "depth" : 6 * mm});
        }
        {
            var Q0;
            Q0=makeQuery(id+"F38.boolean.opBoolean","COPY",FACE,{"derivedFrom":makeQuery(id+"F38.opExtrude","CAP_FACE",FACE,{"disambiguationData":[OSD([sQuery(id+"F37.wireOp",EDGE,"E35.bottom"),sQuery(id+"F37.wireOp",EDGE,"E35.top"),sQuery(id+"F37.wireOp",EDGE,"E35.left"),sQuery(id+"F37.wireOp",EDGE,"E35.right")])],"isStart":false})});
            var sketch = newSketch(context, id + "F47", { "sketchPlane" : qUnion([Q0])});
            skLineSegment(sketch, "E41.bottom", {"start": v(30, -14) * mm, "end": v(14, -14) * mm});
            skLineSegment(sketch, "E41.top", {"start": v(30, -30) * mm, "end": v(14, -30) * mm});
            skLineSegment(sketch, "E41.left", {"start": v(30, -14) * mm, "end": v(30, -30) * mm});
            skLineSegment(sketch, "E41.right", {"start": v(14, -14) * mm, "end": v(14, -30) * mm});
            skSolve(sketch);
        }
        {
            var Q0;
            Q0=qSketchRegion(id+"F47",true);
            extrude(context, id + "F48", {"entities" : qUnion([Q0]), "operationType" : NewBodyOperationType.ADD, "depth" : 6 * mm});
        }
        {
            var Q0;
            Q0=makeQuery(id+"F48.opExtrude","CAP_FACE",FACE,{"disambiguationData":[OSD([sQuery(id+"F47.wireOp",EDGE,"E41.bottom"),sQuery(id+"F47.wireOp",EDGE,"E41.top"),sQuery(id+"F47.wireOp",EDGE,"E41.left"),sQuery(id+"F47.wireOp",EDGE,"E41.right")])],"isStart":false});
            var sketch = newSketch(context, id + "F49", { "sketchPlane" : qUnion([Q0])});
            skCircle(sketch, "E42.cCircle", {"center": v(22.5, -22.5) * mm, "radius": 4 * mm, "construction": true});
            skLineSegment(sketch, "E42.0", {"start": v(26.5, -24.8) * mm, "end": v(22.5, -27.12) * mm});
            skLineSegment(sketch, "E42.1", {"start": v(22.5, -27.12) * mm, "end": v(18.5, -24.8) * mm});
            skLineSegment(sketch, "E42.2", {"start": v(18.5, -24.8) * mm, "end": v(18.5, -20.2) * mm});
            skLineSegment(sketch, "E42.3", {"start": v(18.5, -20.2) * mm, "end": v(22.5, -17.88) * mm});
            skLineSegment(sketch, "E42.4", {"start": v(22.5, -17.88) * mm, "end": v(26.5, -20.2) * mm});
            skLineSegment(sketch, "E42.5", {"start": v(26.5, -20.2) * mm, "end": v(26.5, -24.8) * mm});
            skPoint(sketch, "E42.0.midPoint", {"position": v(24.5, -25.96) * mm});
            skSolve(sketch);
        }
        {
            var Q0;
            Q0=qSketchRegion(id+"F49",true);
            extrude(context, id + "F50", {"entities" : qUnion([Q0]), "operationType" : NewBodyOperationType.REMOVE, "oppositeDirection" : true, "depth" : 6 * mm});
        }
        {
            var Q0;
            Q0=makeQuery(id+"F46.opExtrude","CAP_FACE",FACE,{"disambiguationData":[OSD([sQuery(id+"F45.wireOp",EDGE,"E40.bottom"),sQuery(id+"F45.wireOp",EDGE,"E40.top"),sQuery(id+"F45.wireOp",EDGE,"E40.left"),sQuery(id+"F45.wireOp",EDGE,"E40.right")])],"isStart":false});
            var sketch = newSketch(context, id + "F51", { "sketchPlane" : qUnion([Q0])});
            skCircle(sketch, "E43.cCircle", {"center": v(-22.5, -22.5) * mm, "radius": 4 * mm, "construction": true});
            skLineSegment(sketch, "E43.0", {"start": v(-18.58, -24.94) * mm, "end": v(-22.65, -27.12) * mm});
            skLineSegment(sketch, "E43.1", {"start": v(-22.65, -27.12) * mm, "end": v(-26.57, -24.68) * mm});
            skLineSegment(sketch, "E43.2", {"start": v(-26.57, -24.68) * mm, "end": v(-26.42, -20.06) * mm});
            skLineSegment(sketch, "E43.3", {"start": v(-26.42, -20.06) * mm, "end": v(-22.35, -17.88) * mm});
            skLineSegment(sketch, "E43.4", {"start": v(-22.35, -17.88) * mm, "end": v(-18.43, -20.32) * mm});
            skLineSegment(sketch, "E43.5", {"start": v(-18.43, -20.32) * mm, "end": v(-18.58, -24.94) * mm});
            skPoint(sketch, "E43.0.midPoint", {"position": v(-20.61, -26.03) * mm});
            skSolve(sketch);
        }
        {
            var Q0;
            Q0=qSketchRegion(id+"F51",true);
            extrude(context, id + "F52", {"entities" : qUnion([Q0]), "operationType" : NewBodyOperationType.REMOVE, "oppositeDirection" : true, "depth" : 6 * mm});
        }
        {
            var Q0;
            Q0=makeQuery(id+"F44.opExtrude","CAP_FACE",FACE,{"disambiguationData":[OSD([sQuery(id+"F43.wireOp",EDGE,"E39.bottom"),sQuery(id+"F43.wireOp",EDGE,"E39.top"),sQuery(id+"F43.wireOp",EDGE,"E39.left"),sQuery(id+"F43.wireOp",EDGE,"E39.right")])],"isStart":false});
            var sketch = newSketch(context, id + "F53", { "sketchPlane" : qUnion([Q0])});
            skCircle(sketch, "E44.cCircle", {"center": v(22.5, 22.5) * mm, "radius": 4 * mm, "construction": true});
            skLineSegment(sketch, "E44.0", {"start": v(26.49, 20.17) * mm, "end": v(22.47, 17.88) * mm});
            skLineSegment(sketch, "E44.1", {"start": v(22.47, 17.88) * mm, "end": v(18.49, 20.22) * mm});
            skLineSegment(sketch, "E44.2", {"start": v(18.49, 20.22) * mm, "end": v(18.51, 24.83) * mm});
            skLineSegment(sketch, "E44.3", {"start": v(18.51, 24.83) * mm, "end": v(22.53, 27.12) * mm});
            skLineSegment(sketch, "E44.4", {"start": v(22.53, 27.12) * mm, "end": v(26.51, 24.78) * mm});
            skLineSegment(sketch, "E44.5", {"start": v(26.51, 24.78) * mm, "end": v(26.49, 20.17) * mm});
            skPoint(sketch, "E44.0.midPoint", {"position": v(24.48, 19.02) * mm});
            skSolve(sketch);
        }
        {
            var Q0;
            Q0=qSketchRegion(id+"F53",true);
            extrude(context, id + "F54", {"entities" : qUnion([Q0]), "operationType" : NewBodyOperationType.REMOVE, "oppositeDirection" : true, "depth" : 6 * mm});
        }
        {
            var Q0;
            Q0=makeQuery(id+"F40.opExtrude","SWEPT_EDGE",EDGE,{"disambiguationData":[OSD([sQuery(id+"F39.wireOp",EDGE,"E37.bottom"),sQuery(id+"F39.wireOp",EDGE,"E37.left")])]});
            var Q1;
            Q1=makeQuery(id+"F44.opExtrude","SWEPT_EDGE",EDGE,{"disambiguationData":[OSD([sQuery(id+"F43.wireOp",EDGE,"E39.top"),sQuery(id+"F43.wireOp",EDGE,"E39.right")])]});
            var Q2;
            Q2=makeQuery(id+"F46.opExtrude","SWEPT_EDGE",EDGE,{"disambiguationData":[OSD([sQuery(id+"F45.wireOp",EDGE,"E40.bottom"),sQuery(id+"F45.wireOp",EDGE,"E40.left")])]});
            var Q3;
            Q3=makeQuery(id+"F48.opExtrude","SWEPT_EDGE",EDGE,{"disambiguationData":[OSD([sQuery(id+"F47.wireOp",EDGE,"E41.bottom"),sQuery(id+"F47.wireOp",EDGE,"E41.right")])]});
            fillet(context, id + "F55", {"entities" : qUnion([Q0, Q1, Q2, Q3]), "radius" : 3 * mm, "tangentPropagation" : true, "allowEdgeOverflow" : false});
        }
        {
            var Q0;
            Q0=makeQuery(id+"F38.boolean.opBoolean","COPY",EDGE,{"derivedFrom":makeQuery(id+"F38.opExtrude","SWEPT_EDGE",EDGE,{"disambiguationData":[OSD([sQuery(id+"F37.wireOp",EDGE,"E36.top"),sQuery(id+"F37.wireOp",EDGE,"E36.right")])]})});
            var Q1;
            Q1=makeQuery(id+"F38.boolean.opBoolean","COPY",EDGE,{"derivedFrom":makeQuery(id+"F38.opExtrude","SWEPT_EDGE",EDGE,{"disambiguationData":[OSD([sQuery(id+"F37.wireOp",EDGE,"E33.bottom"),sQuery(id+"F37.wireOp",EDGE,"E33.right")])]})});
            var Q2;
            Q2=makeQuery(id+"F38.boolean.opBoolean","COPY",EDGE,{"derivedFrom":makeQuery(id+"F38.opExtrude","SWEPT_EDGE",EDGE,{"disambiguationData":[OSD([sQuery(id+"F37.wireOp",EDGE,"E33.bottom"),sQuery(id+"F37.wireOp",EDGE,"E33.left")])]})});
            var Q3;
            Q3=makeQuery(id+"F38.boolean.opBoolean","COPY",EDGE,{"derivedFrom":makeQuery(id+"F38.opExtrude","SWEPT_EDGE",EDGE,{"disambiguationData":[OSD([sQuery(id+"F37.wireOp",EDGE,"E33.top"),sQuery(id+"F37.wireOp",EDGE,"E33.left")])]})});
            var Q4;
            Q4=makeQuery(id+"F38.boolean.opBoolean","COPY",EDGE,{"derivedFrom":makeQuery(id+"F38.opExtrude","SWEPT_EDGE",EDGE,{"disambiguationData":[OSD([sQuery(id+"F37.wireOp",EDGE,"E33.top"),sQuery(id+"F37.wireOp",EDGE,"E33.right")])]})});
            var Q5;
            Q5=makeQuery(id+"F38.boolean.opBoolean","COPY",EDGE,{"derivedFrom":makeQuery(id+"F38.opExtrude","SWEPT_EDGE",EDGE,{"disambiguationData":[OSD([sQuery(id+"F37.wireOp",EDGE,"E34.top"),sQuery(id+"F37.wireOp",EDGE,"E34.right")])]})});
            var Q6;
            Q6=makeQuery(id+"F38.boolean.opBoolean","COPY",EDGE,{"derivedFrom":makeQuery(id+"F38.opExtrude","SWEPT_EDGE",EDGE,{"disambiguationData":[OSD([sQuery(id+"F37.wireOp",EDGE,"E34.top"),sQuery(id+"F37.wireOp",EDGE,"E34.left")])]})});
            var Q7;
            Q7=makeQuery(id+"F38.boolean.opBoolean","COPY",EDGE,{"derivedFrom":makeQuery(id+"F38.opExtrude","SWEPT_EDGE",EDGE,{"disambiguationData":[OSD([sQuery(id+"F37.wireOp",EDGE,"E34.bottom"),sQuery(id+"F37.wireOp",EDGE,"E34.right")])]})});
            var Q8;
            Q8=makeQuery(id+"F38.boolean.opBoolean","COPY",EDGE,{"derivedFrom":makeQuery(id+"F38.opExtrude","SWEPT_EDGE",EDGE,{"disambiguationData":[OSD([sQuery(id+"F37.wireOp",EDGE,"E34.bottom"),sQuery(id+"F37.wireOp",EDGE,"E34.left")])]})});
            var Q9;
            Q9=makeQuery(id+"F38.boolean.opBoolean","COPY",EDGE,{"derivedFrom":makeQuery(id+"F38.opExtrude","SWEPT_EDGE",EDGE,{"disambiguationData":[OSD([sQuery(id+"F37.wireOp",EDGE,"E36.bottom"),sQuery(id+"F37.wireOp",EDGE,"E36.left")])]})});
            var Q10;
            Q10=makeQuery(id+"F38.boolean.opBoolean","COPY",EDGE,{"derivedFrom":makeQuery(id+"F38.opExtrude","SWEPT_EDGE",EDGE,{"disambiguationData":[OSD([sQuery(id+"F37.wireOp",EDGE,"E36.bottom"),sQuery(id+"F37.wireOp",EDGE,"E36.right")])]})});
            var Q11;
            Q11=makeQuery(id+"F38.boolean.opBoolean","COPY",EDGE,{"derivedFrom":makeQuery(id+"F38.opExtrude","SWEPT_EDGE",EDGE,{"disambiguationData":[OSD([sQuery(id+"F37.wireOp",EDGE,"E36.top"),sQuery(id+"F37.wireOp",EDGE,"E36.left")])]})});
            var Q12;
            Q12=makeQuery(id+"F38.boolean.opBoolean","COPY",EDGE,{"derivedFrom":makeQuery(id+"F38.opExtrude","SWEPT_EDGE",EDGE,{"disambiguationData":[OSD([sQuery(id+"F37.wireOp",EDGE,"E35.top"),sQuery(id+"F37.wireOp",EDGE,"E35.right")])]})});
            var Q13;
            Q13=makeQuery(id+"F38.boolean.opBoolean","COPY",EDGE,{"derivedFrom":makeQuery(id+"F38.opExtrude","SWEPT_EDGE",EDGE,{"disambiguationData":[OSD([sQuery(id+"F37.wireOp",EDGE,"E35.bottom"),sQuery(id+"F37.wireOp",EDGE,"E35.right")])]})});
            var Q14;
            Q14=makeQuery(id+"F38.boolean.opBoolean","COPY",EDGE,{"derivedFrom":makeQuery(id+"F38.opExtrude","SWEPT_EDGE",EDGE,{"disambiguationData":[OSD([sQuery(id+"F37.wireOp",EDGE,"E35.bottom"),sQuery(id+"F37.wireOp",EDGE,"E35.left")])]})});
            var Q15;
            Q15=makeQuery(id+"F38.boolean.opBoolean","COPY",EDGE,{"derivedFrom":makeQuery(id+"F38.opExtrude","SWEPT_EDGE",EDGE,{"disambiguationData":[OSD([sQuery(id+"F37.wireOp",EDGE,"E35.top"),sQuery(id+"F37.wireOp",EDGE,"E35.left")])]})});
            fillet(context, id + "F56", {"entities" : qUnion([Q0, Q1, Q2, Q3, Q4, Q5, Q6, Q7, Q8, Q9, Q10, Q11, Q12, Q13, Q14, Q15]), "radius" : 2 * mm, "tangentPropagation" : true, "allowEdgeOverflow" : false});
        }
        {
            var Q0;
            Q0=makeQuery(id+"F1.opExtrude","CAP_FACE",FACE,{"disambiguationData":[OSD([sQuery(id+"F0.wireOp",EDGE,"E0.bottom"),sQuery(id+"F0.wireOp",EDGE,"E0.top"),sQuery(id+"F0.wireOp",EDGE,"E0.left"),sQuery(id+"F0.wireOp",EDGE,"E0.right"),sQuery(id+"F0.wireOp",EDGE,"E1"),sQuery(id+"F0.wireOp",EDGE,"E2.bottom")])],"isStart":true});
            var sketch = newSketch(context, id + "F57", { "sketchPlane" : qUnion([Q0])});
            skLineSegment(sketch, "E45.bottom", {"start": v(-7, 15) * mm, "end": v(7, 15) * mm});
            skLineSegment(sketch, "E45.top", {"start": v(-7, -15) * mm, "end": v(7, -15) * mm});
            skLineSegment(sketch, "E45.left", {"start": v(-7, 15) * mm, "end": v(-7, -15) * mm});
            skLineSegment(sketch, "E45.right", {"start": v(7, 15) * mm, "end": v(7, -15) * mm});
            skSolve(sketch);
        }
        {
            var Q0;
            Q0=qSketchRegion(id+"F57",true);
            extrude(context, id + "F58", {"entities" : qUnion([Q0]), "operationType" : NewBodyOperationType.REMOVE, "oppositeDirection" : true, "depth" : 18 * mm});
        }
        {
            var Q0;
            Q0=makeQuery(id+"F1.opExtrude","CAP_FACE",FACE,{"disambiguationData":[OSD([sQuery(id+"F0.wireOp",EDGE,"E0.bottom"),sQuery(id+"F0.wireOp",EDGE,"E0.top"),sQuery(id+"F0.wireOp",EDGE,"E0.left"),sQuery(id+"F0.wireOp",EDGE,"E0.right"),sQuery(id+"F0.wireOp",EDGE,"E1"),sQuery(id+"F0.wireOp",EDGE,"E2.bottom")])],"isStart":true});
            var sketch = newSketch(context, id + "F59", { "sketchPlane" : qUnion([Q0])});
            skLineSegment(sketch, "E46.bottom", {"start": v(-15, 7) * mm, "end": v(15, 7) * mm});
            skLineSegment(sketch, "E46.top", {"start": v(-15, -7) * mm, "end": v(15, -7) * mm});
            skLineSegment(sketch, "E46.left", {"start": v(-15, 7) * mm, "end": v(-15, -7) * mm});
            skLineSegment(sketch, "E46.right", {"start": v(15, 7) * mm, "end": v(15, -7) * mm});
            skSolve(sketch);
        }
        {
            var Q0;
            Q0=qSketchRegion(id+"F59",true);
            extrude(context, id + "F60", {"entities" : qUnion([Q0]), "operationType" : NewBodyOperationType.REMOVE, "oppositeDirection" : true, "depth" : 18 * mm});
        }
        {
            var Q0;
            Q0=makeQuery(id+"F60.boolean.opBoolean","INTERSECT",EDGE,{"derivedFrom":[makeQuery(id+"F58.boolean.opBoolean","COPY",FACE,{"derivedFrom":makeQuery(id+"F58.opExtrude","SWEPT_FACE",FACE,{"disambiguationData":[OSD([sQuery(id+"F57.wireOp",EDGE,"E45.right")])]})}),makeQuery(id+"F60.opExtrude","SWEPT_FACE",FACE,{"disambiguationData":[OSD([sQuery(id+"F59.wireOp",EDGE,"E46.bottom")])]})]});
            var Q1;
            Q1=makeQuery(id+"F60.boolean.opBoolean","INTERSECT",EDGE,{"derivedFrom":[makeQuery(id+"F58.boolean.opBoolean","COPY",FACE,{"derivedFrom":makeQuery(id+"F58.opExtrude","SWEPT_FACE",FACE,{"disambiguationData":[OSD([sQuery(id+"F57.wireOp",EDGE,"E45.left")])]})}),makeQuery(id+"F60.opExtrude","SWEPT_FACE",FACE,{"disambiguationData":[OSD([sQuery(id+"F59.wireOp",EDGE,"E46.bottom")])]})]});
            var Q2;
            Q2=makeQuery(id+"F60.boolean.opBoolean","INTERSECT",EDGE,{"derivedFrom":[makeQuery(id+"F58.boolean.opBoolean","COPY",FACE,{"derivedFrom":makeQuery(id+"F58.opExtrude","SWEPT_FACE",FACE,{"disambiguationData":[OSD([sQuery(id+"F57.wireOp",EDGE,"E45.left")])]})}),makeQuery(id+"F60.opExtrude","SWEPT_FACE",FACE,{"disambiguationData":[OSD([sQuery(id+"F59.wireOp",EDGE,"E46.top")])]})]});
            var Q3;
            Q3=makeQuery(id+"F60.boolean.opBoolean","INTERSECT",EDGE,{"derivedFrom":[makeQuery(id+"F58.boolean.opBoolean","COPY",FACE,{"derivedFrom":makeQuery(id+"F58.opExtrude","SWEPT_FACE",FACE,{"disambiguationData":[OSD([sQuery(id+"F57.wireOp",EDGE,"E45.right")])]})}),makeQuery(id+"F60.opExtrude","SWEPT_FACE",FACE,{"disambiguationData":[OSD([sQuery(id+"F59.wireOp",EDGE,"E46.top")])]})]});
            fillet(context, id + "F61", {"entities" : qUnion([Q0, Q1, Q2, Q3]), "radius" : 1 * mm, "tangentPropagation" : true, "allowEdgeOverflow" : false});
        }
        {
            var Q0;
            Q0=makeQuery(id+"F60.boolean.opBoolean","MERGE",FACE,{"derivedFrom":[makeQuery(id+"F58.boolean.opBoolean","COPY",FACE,{"derivedFrom":makeQuery(id+"F58.opExtrude","CAP_FACE",FACE,{"disambiguationData":[OSD([sQuery(id+"F57.wireOp",EDGE,"E45.bottom"),sQuery(id+"F57.wireOp",EDGE,"E45.top"),sQuery(id+"F57.wireOp",EDGE,"E45.left"),sQuery(id+"F57.wireOp",EDGE,"E45.right")])],"isStart":false})}),makeQuery(id+"F60.opExtrude","CAP_FACE",FACE,{"disambiguationData":[OSD([sQuery(id+"F59.wireOp",EDGE,"E46.bottom"),sQuery(id+"F59.wireOp",EDGE,"E46.top"),sQuery(id+"F59.wireOp",EDGE,"E46.left"),sQuery(id+"F59.wireOp",EDGE,"E46.right")])],"isStart":false})]});
            var sketch = newSketch(context, id + "F62", { "sketchPlane" : qUnion([Q0])});
            skCircle(sketch, "E47", {"center": v(0, 0) * mm, "radius": 10 * mm});
            skSolve(sketch);
        }
        {
            var Q0;
            Q0=qSketchRegion(id+"F62",true);
            extrude(context, id + "F63", {"entities" : qUnion([Q0]), "operationType" : NewBodyOperationType.ADD, "depth" : 6 * mm});
        }
        {
            var Q0;
            Q0=makeQuery(id+"F63.opExtrude","CAP_FACE",FACE,{"disambiguationData":[OSD([sQuery(id+"F62.wireOp",EDGE,"E47")])],"isStart":false});
            var sketch = newSketch(context, id + "F64", { "sketchPlane" : qUnion([Q0])});
            skCircle(sketch, "E48", {"center": v(0, 0) * mm, "radius": 3.5 * mm});
            skSolve(sketch);
        }
        {
            var Q0;
            Q0=qSketchRegion(id+"F64",true);
            extrude(context, id + "F65", {"entities" : qUnion([Q0]), "operationType" : NewBodyOperationType.REMOVE, "oppositeDirection" : true, "depth" : 25 * mm});
        }
    });
